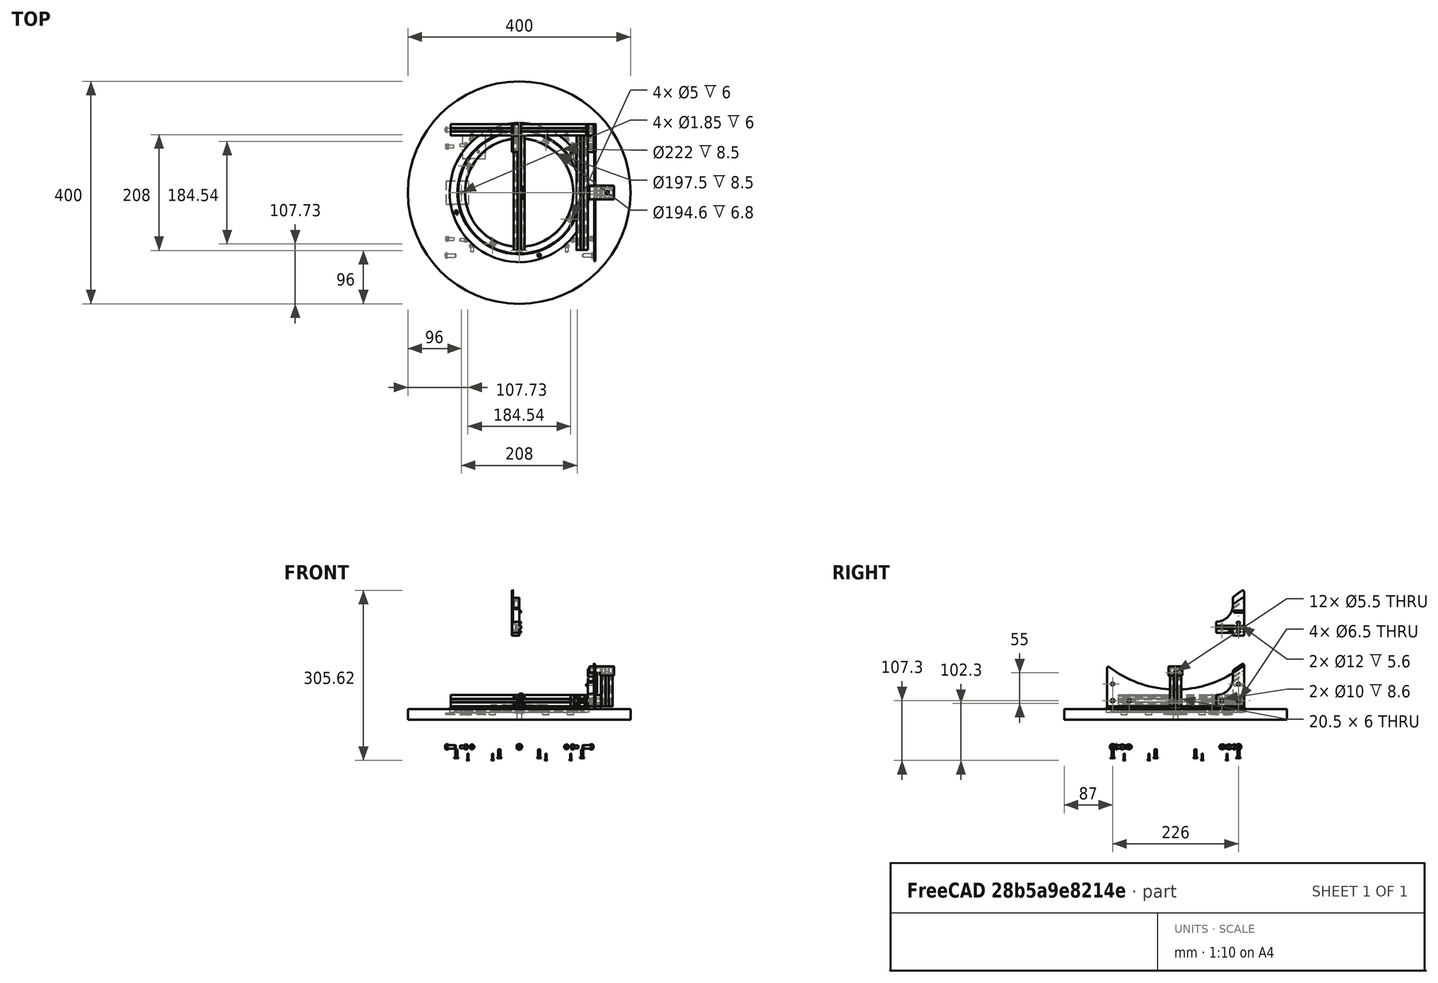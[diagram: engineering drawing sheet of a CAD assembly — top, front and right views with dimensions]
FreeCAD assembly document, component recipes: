
FREECAD ASSEMBLY — COMPONENT RECIPES ("Base")

This assembly document has 22 components, labeled P0..P21 below (a component is one placed body or linked part). 20 of them carry a construction recipe — the FreeCAD feature program that regenerates the part from scratch, quoted from this document or its linked companion documents; the rest are supplied as boundary geometry only. No exploded tour is included for this assembly.
NOTE — this tour is split across 2 documents so each fits a 32k-token context. This is document 1: the component sections continue in the remaining 1 document, each repeating the header above.
COMPONENT P0 — geometry summary ("SlewBearing"; no construction recipe available for this part):
  bounding box: 250.0 x 250.0 x 12.5 mm
  tessellated surface: 11,438 triangles
  volume: 155107 mm^3 (20% of its bounding box)
  symmetry: 4-fold rotationally symmetric about the z axis
COMPONENT P1 — recipe-attached ("RockerPost", modeled in this document).
Construction recipe (the document's own serialized feature program — sketch geometry with constraints, then the solid features built on it; lengths are millimeters unless a unit is written):

FEATURE [PartDesign::ShapeBinder] ShapeBinder012  label="RockerPost_Shapebinder_Rocker"
  Support = -> [Binder]
  TraceSupport = false
FEATURE [Sketcher::SketchObject] Sketch030  label="RockerPost_Sketch"
  ExternalGeometry = -> [ShapeBinder012]
  FullyConstrained = true
  MapMode = 5
  Placement = pos=(0,0,0) rot=(0.57735,0.57735,0.57735;2.0944rad)
  Support = -> [YZ_Plane030]
  sketch-geometry (6):
    g0: LineSegment StartX=103 StartY=43.562 StartZ=0 EndX=103 EndY=-15 EndZ=0
    g1: LineSegment StartX=103 StartY=-15 StartZ=0 EndX=123 EndY=-15 EndZ=0
    g2: LineSegment StartX=123 StartY=-15 StartZ=0 EndX=123 EndY=57.2946 EndZ=0
    g3: ArcOfCircle CenterX=0 CenterY=215 CenterZ=0 NormalX=0 NormalY=0 NormalZ=1 AngleXU=0 Radius=200 StartAngle=5.2534 EndAngle=5.37477
    g4: Circle CenterX=113 CenterY=30 CenterZ=0 NormalX=0 NormalY=0 NormalZ=1 AngleXU=0 Radius=2.75
    g5: Circle CenterX=113 CenterY=7.1e-15 CenterZ=0 NormalX=0 NormalY=0 NormalZ=1 AngleXU=0 Radius=3.25
  constraints (16):
    c: PointOnObject(g0,g-3)
    c: Vertical(g0)
    c: Coincident(g1,g0)
    c: Coincident(g2,g1)
    c: Vertical(g2)
    c: Coincident(g3,g-3)
    c: Coincident(g3,g0)
    c: Coincident(g3,g2)
    c: Symmetric(g0,g1,g-5)
    c: DistanceX(g1,g1) = 20
    c: DistanceY(g1) = -15
    c: DistanceY(g2,g2) = 72.2946  'PostHeight'
    c: Coincident(g4,g-6)
    c: Coincident(g5,g-5)
    c: Diameter(g5) = 6.5
    c: Diameter(g4) = 5.5
FEATURE [PartDesign::Pad] Pad016  label="RockerPost_Pillar"
  Direction = (1,-2e-16,3e-16)
  Length = 7
  Length2 = 5
  Midplane = true
  Placement = pos=(0,0,0) rot=(0.57735,0.57735,0.57735;2.0944rad)
  Profile = -> Sketch030
  Type = 4
  expr: Length = <<Common>>#<<Parameters>>.rail_width / 2 + 2
  expr: Length2 = <<Common>>#<<Parameters>>.rail_width / 2
FEATURE [PartDesign::CoordinateSystem] Local_CS042  label="LCS_RockerPost_H1"
  AttacherType = Attacher::AttachEngine3D
  MapMode = 11
  Placement = pos=(-5,113,6.1e-15) rot=(0.707107,0,-0.707107;3.14159rad)
  Support = -> [Pad016]
FEATURE [PartDesign::CoordinateSystem] Local_CS044  label="LCS_RockerPost_H2"
  AttacherType = Attacher::AttachEngine3D
  MapMode = 11
  Placement = pos=(7,113,9.1e-15) rot=(0.707107,0,0.707107;3.14159rad)
  Support = -> [Pad016]
FEATURE [PartDesign::Plane] DatumPlane010  label="RockerPost_DatumPlane_Top"
  AttachmentOffset = pos=(0,0,72.2946) rot=(0,0,1;0rad)
  Length = 427.613
  MapMode = 5
  Placement = pos=(-1.6e-14,2.52e-14,57.2946) rot=(0,0,-1;1.5708rad)
  ResizeMode = 0
  Support = -> [Pad016]
  Width = 78.2613
  expr: .AttachmentOffset.Base.z = Sketch030.Constraints.PostHeight
FEATURE [Sketcher::SketchObject] Sketch089  label="RockerPost_BraceHole_Sketch"
  ExternalGeometry = -> [Pad016]
  FullyConstrained = true
  MapMode = 5
  Placement = pos=(-5,0,0) rot=(0.57735,0.57735,-0.57735;4.18879rad)
  Support = -> [Pad016]
  expr: Constraints[1] = <<Common>>#<<Parameters>>.sidebolt
  sketch-geometry (1):
    g0: Circle CenterX=0 CenterY=30 CenterZ=0 NormalX=0 NormalY=0 NormalZ=1 AngleXU=0 Radius=2.5
  constraints (3):
    c: PointOnObject(g0,g-2)
    c: Diameter(g0) = 5
    c: DistanceY(g-3,g0) = 30
FEATURE [PartDesign::CoordinateSystem] Local_CS189  label="LCS_RockerBrace_H1"
  AttacherType = Attacher::AttachEngine3D
  MapMode = 11
  Placement = pos=(-5,113,30) rot=(0.707107,0,0.707107;3.14159rad)
  Support = -> [Pad016]
FEATURE [PartDesign::CoordinateSystem] Local_CS190  label="LCS_RockerBrace_H2"
  AttacherType = Attacher::AttachEngine3D
  MapMode = 11
  Placement = pos=(7,113,30) rot=(0.707107,0,0.707107;3.14159rad)
  Support = -> [Pad016]
FEATURE [PartDesign::Body] Body018  label="RockerPost"
  Group = -> [Sketch030,Pad016,Local_CS042,Local_CS044,DatumPlane010,Sketch089,Local_CS189,Local_CS190,ShapeBinder012]
  Origin = -> Origin030
  Placement = pos=(128,0,-132) rot=(0,0,1;0rad)
  Tip = -> Pad016
  expr: .Placement.Base.x = <<Common>>#<<Parameters>>.boxsize_x / 2 + <<Common>>#<<Parameters>>.rail_width / 2
  expr: .Placement.Base.z = <<Common>>#<<Parameters>>.datum_azbase
COMPONENT P2 — recipe-attached ("SidePlate", modeled in this document).
Construction recipe (the document's own serialized feature program — sketch geometry with constraints, then the solid features built on it; lengths are millimeters unless a unit is written):

FEATURE [PartDesign::CoordinateSystem] Local_CS217  label="LCS_SidePlate_ArmSlot"
  AttacherType = Attacher::AttachEngine3D
  AttachmentOffset = pos=(0,-5,1) rot=(0,0,1;1.5708rad)
  MapMode = 5
  Placement = pos=(1,-1.3e-15,-5) rot=(0.707107,0,0.707107;3.14159rad)
  Support = -> [YZ_Plane032]
  expr: .AttachmentOffset.Base.z = <<Common>>#<<Parameters>>.rocker_plate / 2
FEATURE [PartDesign::Plane] DatumPlane029  label="SidePlate_DatumPlane_P"
  AttachmentOffset = pos=(0,0,2) rot=(0,0,1;0rad)
  Length = 275.092
  MapMode = 5
  Placement = pos=(2,-4e-16,4e-16) rot=(0.57735,0.57735,0.57735;2.0944rad)
  ResizeMode = 0
  Support = -> [YZ_Plane032]
  Width = 115.103
  expr: .AttachmentOffset.Base.z = <<Common>>#<<Parameters>>.rocker_plate
FEATURE [PartDesign::CoordinateSystem] Local_CS059  label="LCS_SidePlate_PostAP"
  AttacherType = Attacher::AttachEngine3D
  AttachmentOffset = pos=(113,-5,0) rot=(0,0,1;1.5708rad)
  MapMode = 5
  Placement = pos=(2,113,-5) rot=(0.707107,0,0.707107;3.14159rad)
  Support = -> [DatumPlane029]
  expr: .AttachmentOffset.Base.x = <<Common>>#<<Parameters>>.bolt_y
FEATURE [PartDesign::CoordinateSystem] Local_CS063  label="LCS_SidePlate_PostFP"
  AttacherType = Attacher::AttachEngine3D
  AttachmentOffset = pos=(-113,-5,0) rot=(0,0,1;1.5708rad)
  MapMode = 5
  Placement = pos=(2,-113,-5) rot=(0.707107,0,0.707107;3.14159rad)
  Support = -> [DatumPlane029]
  expr: .AttachmentOffset.Base.x = -<<Common>>#<<Parameters>>.bolt_y
FEATURE [PartDesign::CoordinateSystem] Local_CS110  label="LCS_SidePlate_BraceAP"
  AttacherType = Attacher::AttachEngine3D
  AttachmentOffset = pos=(83,-5,0) rot=(0,0,1;1.5708rad)
  MapMode = 5
  Placement = pos=(2,83,-5) rot=(0.707107,0,0.707107;3.14159rad)
  Support = -> [DatumPlane029]
  expr: .AttachmentOffset.Base.x = <<Common>>#<<Parameters>>.bolt_y - 30
FEATURE [PartDesign::CoordinateSystem] Local_CS112  label="LCS_SidePlate_BraceFP"
  AttacherType = Attacher::AttachEngine3D
  AttachmentOffset = pos=(-83,-5,0) rot=(0,0,1;1.5708rad)
  MapMode = 5
  Placement = pos=(2,-83,-5) rot=(0.707107,0,0.707107;3.14159rad)
  Support = -> [DatumPlane029]
  expr: .AttachmentOffset.Base.x = -<<Common>>#<<Parameters>>.bolt_y + 30
FEATURE [PartDesign::CoordinateSystem] Local_CS182  label="LCS_SidePlate_PBrace_AP"
  AttacherType = Attacher::AttachEngine3D
  AttachmentOffset = pos=(113,25,0) rot=(0,0,1;1.5708rad)
  MapMode = 5
  Placement = pos=(2,113,25) rot=(0.707107,0,0.707107;3.14159rad)
  Support = -> [DatumPlane029]
  expr: .AttachmentOffset.Base.x = <<Common>>#<<Parameters>>.bolt_y
FEATURE [PartDesign::CoordinateSystem] Local_CS184  label="LCS_SidePlate_PBrace_FP"
  AttacherType = Attacher::AttachEngine3D
  AttachmentOffset = pos=(-113,25,0) rot=(0,0,1;1.5708rad)
  MapMode = 5
  Placement = pos=(2,-113,25) rot=(0.707107,0,0.707107;3.14159rad)
  Support = -> [DatumPlane029]
  expr: .AttachmentOffset.Base.x = -<<Common>>#<<Parameters>>.bolt_y
FEATURE [PartDesign::Plane] DatumPlane030  label="SidePlate_DatumPlane_S"
  Length = 275.092
  MapMode = 5
  Placement = pos=(0,0,0) rot=(0.57735,0.57735,0.57735;2.0944rad)
  ResizeMode = 0
  Support = -> [YZ_Plane032]
  Width = 115.103
FEATURE [PartDesign::CoordinateSystem] Local_CS061  label="LCS_SidePlate_PostAS"
  AttacherType = Attacher::AttachEngine3D
  AttachmentOffset = pos=(-113,-5,0) rot=(0,0,1;1.5708rad)
  MapMode = 5
  Placement = pos=(1.31e-14,113,-5) rot=(0,1,0;4.71239rad)
  Support = -> [DatumPlane030]
  expr: .AttachmentOffset.Base.x = -<<Common>>#<<Parameters>>.bolt_y
FEATURE [PartDesign::CoordinateSystem] Local_CS065  label="LCS_SidePlate_PostFS"
  AttacherType = Attacher::AttachEngine3D
  AttachmentOffset = pos=(113,-5,0) rot=(0,0,1;1.5708rad)
  MapMode = 5
  Placement = pos=(-1.2e-14,-113,-5) rot=(0,1,0;4.71239rad)
  Support = -> [DatumPlane030]
  expr: .AttachmentOffset.Base.x = <<Common>>#<<Parameters>>.bolt_y
FEATURE [PartDesign::CoordinateSystem] Local_CS111  label="LCS_SidePlate_BraceAS"
  AttacherType = Attacher::AttachEngine3D
  AttachmentOffset = pos=(-83,-5,0) rot=(0,0,1;1.5708rad)
  MapMode = 5
  Placement = pos=(9.8e-15,83,-5) rot=(0,1,0;4.71239rad)
  Support = -> [DatumPlane030]
  expr: .AttachmentOffset.Base.x = -<<Common>>#<<Parameters>>.bolt_y + 30
FEATURE [PartDesign::CoordinateSystem] Local_CS113  label="LCS_SidePlate_BraceFS"
  AttacherType = Attacher::AttachEngine3D
  AttachmentOffset = pos=(83,-5,0) rot=(0,0,1;1.5708rad)
  MapMode = 5
  Placement = pos=(-8.7e-15,-83,-5) rot=(0,1,0;4.71239rad)
  Support = -> [DatumPlane030]
  expr: .AttachmentOffset.Base.x = <<Common>>#<<Parameters>>.bolt_y - 30
FEATURE [PartDesign::CoordinateSystem] Local_CS183  label="LCS_SidePlate_PBrace_AS"
  AttacherType = Attacher::AttachEngine3D
  AttachmentOffset = pos=(-113,25,0) rot=(0,0,1;1.5708rad)
  MapMode = 5
  Placement = pos=(9.8e-15,113,25) rot=(0,1,0;4.71239rad)
  Support = -> [DatumPlane030]
  expr: .AttachmentOffset.Base.x = -<<Common>>#<<Parameters>>.bolt_y
FEATURE [PartDesign::CoordinateSystem] Local_CS185  label="LCS_SidePlate_PBrace_FS"
  AttacherType = Attacher::AttachEngine3D
  AttachmentOffset = pos=(113,25,0) rot=(0,0,1;1.5708rad)
  MapMode = 5
  Placement = pos=(-1.53e-14,-113,25) rot=(0,1,0;4.71239rad)
  Support = -> [DatumPlane030]
  expr: .AttachmentOffset.Base.x = <<Common>>#<<Parameters>>.bolt_y
FEATURE [Sketcher::SketchObject] Sketch274  label="RockerSide_MasterSketch"
  FullyConstrained = true
  MapMode = 5
  Placement = pos=(0,0,0) rot=(0.57735,0.57735,0.57735;2.0944rad)
  Support = -> [YZ_Plane032]
  expr: Constraints[12] = <<Common>>#<<Parameters>>.datum_lowercell - <<Common>>#<<Parameters>>.datum_rocker_z
  expr: Constraints[13] = <<Common>>#<<Parameters>>.bolt_y
  expr: Constraints[1] = <<Common>>#<<Parameters>>.rail_dia
  expr: Constraints[2] = <<Common>>#<<Parameters>>.datum_rocker_z - <<Common>>#<<Parameters>>.datum_azbase
  expr: Constraints[33] = <<Common>>#<<Parameters>>.rail_dia - <<Common>>#<<Parameters>>.rail_height * 2
  expr: Constraints[6] = <<Common>>#<<Parameters>>.bolt_y
  sketch-geometry (14):
    g0: Circle CenterX=0 CenterY=215 CenterZ=0 NormalX=0 NormalY=0 NormalZ=1 AngleXU=0 Radius=200
    g1: Circle CenterX=0 CenterY=0 CenterZ=0 NormalX=0 NormalY=0 NormalZ=1 AngleXU=0 Radius=2.5
    g2: Circle CenterX=-113 CenterY=0 CenterZ=0 NormalX=0 NormalY=0 NormalZ=1 AngleXU=0 Radius=3
    g3: Circle CenterX=113 CenterY=0 CenterZ=0 NormalX=0 NormalY=0 NormalZ=1 AngleXU=0 Radius=3
    g4: Circle CenterX=113 CenterY=30 CenterZ=0 NormalX=0 NormalY=0 NormalZ=1 AngleXU=0 Radius=2.5
    g5: Circle CenterX=-113 CenterY=30 CenterZ=0 NormalX=0 NormalY=0 NormalZ=1 AngleXU=0 Radius=2.5
    g6: Circle CenterX=-113 CenterY=70 CenterZ=0 NormalX=0 NormalY=0 NormalZ=1 AngleXU=0 Radius=2.5
    g7: Circle CenterX=0 CenterY=31.1686 CenterZ=0 NormalX=0 NormalY=0 NormalZ=1 AngleXU=0 Radius=2.5
    g8: Circle CenterX=113 CenterY=70 CenterZ=0 NormalX=0 NormalY=0 NormalZ=1 AngleXU=0 Radius=2.5
    g9: Circle CenterX=0 CenterY=215 CenterZ=0 NormalX=0 NormalY=0 NormalZ=1 AngleXU=0 Radius=183.831
    g10: GeomPoint X=113 Y=70 Z=0
    g11: LineSegment StartX=-113 StartY=0 StartZ=0 EndX=-113 EndY=70 EndZ=0
    g12: LineSegment StartX=113 StartY=0 StartZ=0 EndX=113 EndY=70 EndZ=0
    g13: Circle CenterX=0 CenterY=215 CenterZ=0 NormalX=0 NormalY=0 NormalZ=1 AngleXU=0 Radius=165
  constraints (34):
    c: PointOnObject(g0,g-2)
    c: Diameter(g0) = 400
    c: DistanceY(g0) = 215
    c: Coincident(g1,g-1)
    c: PointOnObject(g3,g-1)
    c: PointOnObject(g7,g-2)
    c: DistanceX(g3) = 113
    c: Symmetric(g3,g2,g-2)
    c: Diameter(g2) = 6
    c: Equal(g2,g3)
    c: Coincident(g9,g0)
    c: PointOnObject(g10,g9)
    c: DistanceY(g0,g10) = -145
    c: DistanceX(g0,g10) = 113
    c: Diameter(g1) = 5
    c: Coincident(g11,g2)
    c: PointOnObject(g11,g9)
    c: Coincident(g12,g3)
    c: PointOnObject(g12,g9)
    c: Vertical(g12)
    c: Vertical(g11)
    c: PointOnObject(g5,g11)
    c: Coincident(g6,g11)
    c: PointOnObject(g7,g9)
    c: Coincident(g8,g12)
    c: Equal(g4,g8)
    c: Equal(g8,g7)
    c: Equal(g7,g6)
    c: Equal(g6,g5)
    c: Equal(g5,g1)
    c: Symmetric(g4,g5,g-2)
    c: DistanceY(g4) = 30
    c: Coincident(g13,g0)
    c: Diameter(g13) = 330
FEATURE [PartDesign::ShapeBinder] ShapeBinder011  label="SidePlate_ShapeBinder_Rocker"
  Support = -> [Binder]
  TraceSupport = false
FEATURE [Sketcher::SketchObject] Sketch035  label="SidePlate_Sketch"
  ExternalGeometry = -> [ShapeBinder011]
  FullyConstrained = true
  MapMode = 5
  Placement = pos=(0,0,0) rot=(0.57735,0.57735,0.57735;2.0944rad)
  Support = -> [YZ_Plane032]
  expr: Constraints[11] = <<Common>>#<<Parameters>>.rail_dia - 10
  expr: Constraints[16] = <<Common>>#<<Parameters>>.pri_fillet
  expr: Constraints[37] = <<Common>>#<<Parameters>>.pri_fillet
  expr: Constraints[5] = <<Common>>#<<Parameters>>.boxsize_y
  sketch-geometry (19):
    g0: LineSegment StartX=-123 StartY=-10 StartZ=0 EndX=123 EndY=-10 EndZ=0
    g1: LineSegment StartX=123 StartY=-10 StartZ=0 EndX=123 EndY=58.52 EndZ=0
    g2: LineSegment StartX=-123 StartY=58.52 StartZ=0 EndX=-123 EndY=-10 EndZ=0
    g3: LineSegment StartX=-113 StartY=1.42e-14 StartZ=0 EndX=113 EndY=1.25e-14 EndZ=0
    g4: Circle CenterX=-113 CenterY=1.42e-14 CenterZ=0 NormalX=0 NormalY=0 NormalZ=1 AngleXU=0 Radius=3.25
    g5: Circle CenterX=113 CenterY=1.25e-14 CenterZ=0 NormalX=0 NormalY=0 NormalZ=1 AngleXU=0 Radius=3.25
    g6: ArcOfCircle CenterX=-2.39e-14 CenterY=215 CenterZ=0 NormalX=0 NormalY=0 NormalZ=1 AngleXU=0 Radius=195 StartAngle=4.05617 EndAngle=5.36861
    g7: Circle CenterX=-83 CenterY=1.25e-14 CenterZ=0 NormalX=0 NormalY=0 NormalZ=1 AngleXU=0 Radius=2.75
    g8: Circle CenterX=83 CenterY=1.25e-14 CenterZ=0 NormalX=0 NormalY=0 NormalZ=1 AngleXU=0 Radius=2.75
    g9: ArcOfCircle CenterX=120.5 CenterY=58.52 CenterZ=0 NormalX=0 NormalY=0 NormalZ=1 AngleXU=0 Radius=2.5 StartAngle=1e-15 EndAngle=2.22702
    g10: Circle CenterX=113 CenterY=30 CenterZ=0 NormalX=0 NormalY=0 NormalZ=1 AngleXU=0 Radius=2.75
    g11: Circle CenterX=-113 CenterY=30 CenterZ=0 NormalX=0 NormalY=0 NormalZ=1 AngleXU=0 Radius=2.75
    g12: LineSegment StartX=-113 StartY=30 StartZ=0 EndX=-113 EndY=1.42e-14 EndZ=0
    g13: LineSegment StartX=-10.25 StartY=3 StartZ=0 EndX=10.25 EndY=3 EndZ=0
    g14: LineSegment StartX=10.25 StartY=3 StartZ=0 EndX=10.25 EndY=-3 EndZ=0
    g15: LineSegment StartX=10.25 StartY=-3 StartZ=0 EndX=-10.25 EndY=-3 EndZ=0
    g16: LineSegment StartX=-10.25 StartY=-3 StartZ=0 EndX=-10.25 EndY=3 EndZ=0
    g17: Circle CenterX=-113 CenterY=70 CenterZ=0 NormalX=0 NormalY=0 NormalZ=1 AngleXU=0 Radius=5.5
    g18: ArcOfCircle CenterX=-120.5 CenterY=58.52 CenterZ=0 NormalX=0 NormalY=0 NormalZ=1 AngleXU=0 Radius=2.5 StartAngle=0.914576 EndAngle=3.14159
  constraints (44):
    c: Coincident(g0,g1)
    c: Coincident(g2,g0)
    c: Vertical(g1)
    c: Vertical(g2)
    c: Symmetric(g0,g0,g-2)
    c: DistanceX(g0,g0) = 246
    c: Symmetric(g3,g3,g-2)
    c: Diameter(g4) = 6.5
    c: Symmetric(g5,g4,g-2)
    c: Symmetric(g7,g8,g-2)
    c: PointOnObject(g7,g3)
    c: Diameter(g6) = 390
    c: DistanceY(g0) = -10
    c: Coincident(g3,g4)
    c: Tangent(g6,g9) = 1.5708
    c: Tangent(g1,g9) = -1.5708
    c: Radius(g9) = 2.5
    c: DistanceX(g8,g5) = 30
    c: Symmetric(g11,g10,g-2)
    c: Equal(g10,g11)
    c: Coincident(g12,g11)
    c: Coincident(g12,g4)
    c: Coincident(g13,g14)
    c: Coincident(g14,g15)
    c: Coincident(g15,g16)
    c: Coincident(g16,g13)
    c: Horizontal(g13)
    c: Vertical(g14)
    c: DistanceX(g15,g15) = 20.5
    c: Symmetric(g14,g15,g-2)
    c: Symmetric(g15,g13,g3)
    c: DistanceY(g16,g16) = 6
    c: Equal(g10,g8)
    c: Equal(g8,g7)
    c: Diameter(g11) = 5.5
    c: Equal(g4,g5)
    c: Diameter(g17) = 11
    c: Radius(g18) = 2.5
    c: Tangent(g18,g2) = -1.5708
    c: Tangent(g18,g6) = 1.5708
    c: Coincident(g17,g-6)
    c: Coincident(g6,g-3)
    c: Coincident(g5,g-8)
    c: Coincident(g10,g-7)
FEATURE [PartDesign::Pad] Pad019  label="SidePlate_Pad"
  Direction = (1,-2e-16,3e-16)
  Length = 2
  Length2 = 100
  Placement = pos=(0,0,0) rot=(0.57735,0.57735,0.57735;2.0944rad)
  Profile = -> Sketch035
  Type = 0
  expr: Length = <<Common>>#<<Parameters>>.rocker_plate
FEATURE [PartDesign::Body] Body020  label="SidePlate"
  Group = -> [Sketch035,Pad019,Local_CS059,Local_CS061,Local_CS063,Local_CS065,Local_CS110,Local_CS111,Local_CS112,Local_CS113,Local_CS182,Local_CS183,Local_CS184,Local_CS185,Local_CS217,DatumPlane029,DatumPlane030,Sketch274,ShapeBinder011]
  Origin = -> Origin032
  Placement = pos=(135,0,-132) rot=(0,0,1;0rad)
  Tip = -> Pad019
  expr: .Placement.Base.x = <<Common>>#<<Parameters>>.boxsize_x / 2 + <<Common>>#<<Parameters>>.rail_width + 2
  expr: .Placement.Base.z = <<Common>>#<<Parameters>>.datum_azbase
COMPONENT P3 — recipe-attached ("ArmSpacer", modeled in this document).
Construction recipe (the document's own serialized feature program — sketch geometry with constraints, then the solid features built on it; lengths are millimeters unless a unit is written):

FEATURE [Sketcher::SketchObject] Sketch096  label="ArmSpacer_Sketch"
  FullyConstrained = true
  MapMode = 5
  Support = -> [XY_Plane069]
  expr: .Constraints.SpacerThick = <<Common>>#<<Parameters>>.alt_sideclamp
  sketch-geometry (12):
    g0: LineSegment StartX=-2 StartY=10 StartZ=0 EndX=11 EndY=10 EndZ=0
    g1: LineSegment StartX=11 StartY=10 StartZ=0 EndX=11 EndY=3 EndZ=0
    g2: LineSegment StartX=11 StartY=3 StartZ=0 EndX=12.5 EndY=3 EndZ=0
    g3: LineSegment StartX=12.5 StartY=3 StartZ=0 EndX=12.5 EndY=-3 EndZ=0
    g4: LineSegment StartX=12.5 StartY=-3 StartZ=0 EndX=11 EndY=-3 EndZ=0
    g5: LineSegment StartX=11 StartY=-3 StartZ=0 EndX=11 EndY=-10 EndZ=0
    g6: LineSegment StartX=11 StartY=-10 StartZ=0 EndX=-2 EndY=-10 EndZ=0
    g7: LineSegment StartX=-2 StartY=10 StartZ=0 EndX=-2 EndY=3 EndZ=0
    g8: LineSegment StartX=-2 StartY=3 StartZ=0 EndX=0 EndY=3 EndZ=0
    g9: LineSegment StartX=0 StartY=3 StartZ=0 EndX=0 EndY=-3 EndZ=0
    g10: LineSegment StartX=0 StartY=-3 StartZ=0 EndX=-2 EndY=-3 EndZ=0
    g11: LineSegment StartX=-2 StartY=-3 StartZ=0 EndX=-2 EndY=-10 EndZ=0
  constraints (35):
    c: Horizontal(g0)
    c: Vertical(g1)
    c: Coincident(g2,g1)
    c: Horizontal(g2)
    c: Coincident(g3,g2)
    c: Coincident(g4,g3)
    c: Coincident(g5,g4)
    c: Vertical(g5)
    c: Coincident(g6,g5)
    c: Horizontal(g6)
    c: Coincident(g0,g1)
    c: DistanceY(g3,g3) = 6
    c: Horizontal(g4)
    c: Equal(g6,g0)
    c: Symmetric(g2,g3,g-1)
    c: DistanceX(g1) = 11  'SpacerThick'
    c: DistanceX(g2,g2) = 1.5
    c: DistanceY(g5,g0) = 20
    c: Equal(g1,g5)
    c: Coincident(g7,g0)
    c: Vertical(g7)
    c: Coincident(g8,g7)
    c: PointOnObject(g8,g-2)
    c: Coincident(g9,g8)
    c: PointOnObject(g9,g-2)
    c: Coincident(g10,g9)
    c: Horizontal(g10)
    c: Coincident(g11,g10)
    c: Coincident(g11,g6)
    c: Vertical(g11)
    c: PointOnObject(g10,g7)
    c: DistanceX(g0,g-1) = 2
    c: PointOnObject(g8,g2)
    c: PointOnObject(g9,g4)
    c: Horizontal(g8)
FEATURE [PartDesign::Pad] Pad035  label="ArmSpacer_Base"
  Direction = (0,0,1)
  Length = 20
  Length2 = 100
  Midplane = true
  Profile = -> Sketch096
  Type = 0
FEATURE [Sketcher::SketchObject] Sketch097  label="ArmSpacer_Tab_Sketch"
  ExternalGeometry = -> [Pad035]
  FullyConstrained = true
  MapMode = 5
  Placement = pos=(0,0,0) rot=(1,0,0;1.5708rad)
  Support = -> [XZ_Plane069]
  sketch-geometry (14):
    g0: LineSegment StartX=0 StartY=-3 StartZ=0 EndX=0 EndY=-10 EndZ=0
    g1: LineSegment StartX=0 StartY=-10 StartZ=0 EndX=-2 EndY=-10 EndZ=0
    g2: LineSegment StartX=-2 StartY=-10 StartZ=0 EndX=-2 EndY=-3 EndZ=0
    g3: LineSegment StartX=-2 StartY=-3 StartZ=0 EndX=0 EndY=-3 EndZ=0
    g4: LineSegment StartX=-2 StartY=10 StartZ=0 EndX=0 EndY=10 EndZ=0
    g5: LineSegment StartX=0 StartY=10 StartZ=0 EndX=0 EndY=3 EndZ=0
    g6: LineSegment StartX=0 StartY=3 StartZ=0 EndX=-2 EndY=3 EndZ=0
    g7: LineSegment StartX=-2 StartY=3 StartZ=0 EndX=-2 EndY=10 EndZ=0
    g8: LineSegment StartX=11 StartY=3 StartZ=0 EndX=12.5 EndY=3 EndZ=0
    g9: LineSegment StartX=12.5 StartY=3 StartZ=0 EndX=12.5 EndY=-3 EndZ=0
    g10: LineSegment StartX=12.5 StartY=-3 StartZ=0 EndX=11 EndY=-3 EndZ=0
    g11: LineSegment StartX=11 StartY=-3 StartZ=0 EndX=11 EndY=3 EndZ=0
    g12: LineSegment StartX=0 StartY=3 StartZ=0 EndX=11 EndY=3 EndZ=0
    g13: LineSegment StartX=0 StartY=-3 StartZ=0 EndX=11 EndY=-3 EndZ=0
  constraints (37):
    c: PointOnObject(g0,g-2)
    c: PointOnObject(g0,g-2)
    c: Coincident(g1,g0)
    c: Coincident(g1,g-3)
    c: Coincident(g2,g1)
    c: PointOnObject(g2,g-3)
    c: Coincident(g3,g2)
    c: Coincident(g3,g0)
    c: Coincident(g4,g5)
    c: Coincident(g5,g6)
    c: Coincident(g6,g7)
    c: Coincident(g7,g4)
    c: Horizontal(g4)
    c: Horizontal(g6)
    c: Vertical(g5)
    c: Vertical(g7)
    c: Coincident(g4,g-3)
    c: PointOnObject(g5,g-2)
    c: Coincident(g8,g9)
    c: Coincident(g9,g10)
    c: Coincident(g10,g11)
    c: Coincident(g11,g8)
    c: Vertical(g9)
    c: PointOnObject(g8,g-4)
    c: PointOnObject(g9,g-5)
    c: Symmetric(g8,g10,g-1)
    c: DistanceY(g11,g11) = 6
    c: Coincident(g12,g5)
    c: Coincident(g12,g8)
    c: Coincident(g13,g0)
    c: Coincident(g13,g10)
    c: Horizontal(g13)
    c: Horizontal(g12)
    c: Horizontal(g1)
    c: Horizontal(g3)
    c: Parallel(g8,g10)
    c: Perpendicular(g-4,g8)
FEATURE [Sketcher::SketchObject] Sketch098  label="ArmSpacer_Hole_Sketch"
  FullyConstrained = true
  MapMode = 5
  Placement = pos=(0,0,0) rot=(0.57735,0.57735,0.57735;2.0944rad)
  Support = -> [YZ_Plane069]
  sketch-geometry (1):
    g0: Circle CenterX=0 CenterY=0 CenterZ=0 NormalX=0 NormalY=0 NormalZ=1 AngleXU=0 Radius=2.75
  constraints (2):
    c: Coincident(g0,g-1)
    c: Diameter(g0) = 5.5
FEATURE [PartDesign::Pocket] Pocket055  label="ArmSpacer_Tab"
  BaseFeature = -> Pad035
  Direction = (0,1,2e-16)
  Length = 5
  Length2 = 100
  Midplane = true
  Profile = -> Sketch097
  Type = 1
FEATURE [PartDesign::Pocket] Pocket056  label="ArmSpacer_Hole"
  BaseFeature = -> Pocket055
  Direction = (-1,2e-16,-3e-16)
  Length = 5
  Length2 = 100
  Midplane = true
  Profile = -> Sketch098
  Type = 1
FEATURE [PartDesign::CoordinateSystem] Local_CS212  label="LCS_ArmSpacer_I"
  AttacherType = Attacher::AttachEngine3D
  MapMode = 11
  Placement = pos=(0,0,1.8e-15) rot=(0.707107,0,0.707107;3.14159rad)
  Support = -> [Pocket056]
FEATURE [PartDesign::CoordinateSystem] Local_CS213  label="LCS_ArmSpacer_O"
  AttacherType = Attacher::AttachEngine3D
  MapMode = 11
  Placement = pos=(11,-2.2e-15,4.2e-15) rot=(0.707107,0,0.707107;3.14159rad)
  Support = -> [Pocket056]
FEATURE [PartDesign::Body] Body022016  label="ArmSpacer"
  Group = -> [Sketch096,Pad035,Sketch097,Sketch098,Local_CS212,Local_CS213,Pocket055,Pocket056]
  Origin = -> Origin069
  Placement = pos=(137,0,-132) rot=(0,0,1;0rad)
  Tip = -> Pocket056
  expr: .Placement.Base.x = <<Common>>#<<Parameters>>.bolt_x + <<Common>>#<<Parameters>>.rail_width + 12 + <<Common>>#<<Parameters>>.rocker_plate
  expr: .Placement.Base.z = <<Common>>#<<Parameters>>.datum_azbase
COMPONENT P4 — recipe-attached ("ArmPost", modeled in this document).
Construction recipe (the document's own serialized feature program — sketch geometry with constraints, then the solid features built on it; lengths are millimeters unless a unit is written):

FEATURE [Sketcher::SketchObject] Sketch099  label="ArmPost_Sketch"
  FullyConstrained = true
  MapMode = 5
  Support = -> [XY_Plane070]
  sketch-geometry (75):
    g0: LineSegment StartX=3 StartY=10 StartZ=0 EndX=3 EndY=8 EndZ=0
    g1: LineSegment StartX=3 StartY=8 StartZ=0 EndX=6 EndY=8 EndZ=0
    g2: LineSegment StartX=2.58579 StartY=4 StartZ=0 EndX=-2.58579 EndY=4 EndZ=0
    g3: LineSegment StartX=-6 StartY=8 StartZ=0 EndX=-3 EndY=8 EndZ=0
    g4: LineSegment StartX=-3 StartY=8 StartZ=0 EndX=-3 EndY=10 EndZ=0
    g5: Circle CenterX=0 CenterY=0 CenterZ=0 NormalX=0 NormalY=0 NormalZ=1 AngleXU=0 Radius=2.1
    g6: LineSegment StartX=-10 StartY=3 StartZ=0 EndX=-8 EndY=3 EndZ=0
    g7: LineSegment StartX=-8 StartY=3 StartZ=0 EndX=-8 EndY=6 EndZ=0
    g8: LineSegment StartX=-4 StartY=2.58579 StartZ=0 EndX=-4 EndY=-2.58579 EndZ=0
    g9: LineSegment StartX=-8 StartY=-6 StartZ=0 EndX=-8 EndY=-3 EndZ=0
    g10: LineSegment StartX=-8 StartY=-3 StartZ=0 EndX=-10 EndY=-3 EndZ=0
    g11: LineSegment StartX=-3 StartY=-10 StartZ=0 EndX=-3 EndY=-8 EndZ=0
    g12: LineSegment StartX=-3 StartY=-8 StartZ=0 EndX=-6 EndY=-8 EndZ=0
    g13: LineSegment StartX=-2.58579 StartY=-4 StartZ=0 EndX=2.58579 EndY=-4 EndZ=0
    g14: LineSegment StartX=6 StartY=-8 StartZ=0 EndX=3 EndY=-8 EndZ=0
    g15: LineSegment StartX=3 StartY=-8 StartZ=0 EndX=3 EndY=-10 EndZ=0
    g16: LineSegment StartX=10 StartY=-3 StartZ=0 EndX=8 EndY=-3 EndZ=0
    g17: LineSegment StartX=8 StartY=-3 StartZ=0 EndX=8 EndY=-6 EndZ=0
    g18: LineSegment StartX=8 StartY=-6 StartZ=0 EndX=7.41421 EndY=-6 EndZ=0
    g19: LineSegment StartX=7.41421 StartY=-6 StartZ=0 EndX=4 EndY=-2.58579 EndZ=0
    g20: LineSegment StartX=4 StartY=-2.58579 StartZ=0 EndX=4 EndY=2.58579 EndZ=0
    g21: LineSegment StartX=4 StartY=2.58579 StartZ=0 EndX=7.41421 EndY=6 EndZ=0
    g22: LineSegment StartX=7.41421 StartY=6 StartZ=0 EndX=8 EndY=6 EndZ=0
    g23: LineSegment StartX=8 StartY=6 StartZ=0 EndX=8 EndY=3 EndZ=0
    g24: LineSegment StartX=8 StartY=3 StartZ=0 EndX=10 EndY=3 EndZ=0
    g25: LineSegment StartX=6 StartY=8 StartZ=0 EndX=6 EndY=7.41421 EndZ=0
    g26: LineSegment StartX=6 StartY=7.41421 StartZ=0 EndX=2.58579 EndY=4 EndZ=0
    g27: LineSegment StartX=-2.58579 StartY=4 StartZ=0 EndX=-6 EndY=7.41421 EndZ=0
    g28: LineSegment StartX=-6 StartY=7.41421 StartZ=0 EndX=-6 EndY=8 EndZ=0
    g29: LineSegment StartX=-8 StartY=6 StartZ=0 EndX=-7.41421 EndY=6 EndZ=0
    g30: LineSegment StartX=-7.41421 StartY=6 StartZ=0 EndX=-4 EndY=2.58579 EndZ=0
    g31: LineSegment StartX=-4 StartY=-2.58579 StartZ=0 EndX=-7.41421 EndY=-6 EndZ=0
    g32: LineSegment StartX=-7.41421 StartY=-6 StartZ=0 EndX=-8 EndY=-6 EndZ=0
    g33: LineSegment StartX=-2.58579 StartY=-4 StartZ=0 EndX=-6 EndY=-7.41421 EndZ=0
    g34: LineSegment StartX=-6 StartY=-7.41421 StartZ=0 EndX=-6 EndY=-8 EndZ=0
    g35: LineSegment StartX=2.58579 StartY=-4 StartZ=0 EndX=6 EndY=-7.41421 EndZ=0
    g36: LineSegment StartX=6 StartY=-7.41421 StartZ=0 EndX=6 EndY=-8 EndZ=0
    g37: LineSegment StartX=-4 StartY=2.58579 StartZ=0 EndX=-2.58579 EndY=4 EndZ=0
    g38: LineSegment StartX=-7.41421 StartY=7.41421 StartZ=0 EndX=7.41421 EndY=7.41421 EndZ=0
    g39: LineSegment StartX=7.41421 StartY=7.41421 StartZ=0 EndX=7.41421 EndY=-7.41421 EndZ=0
    g40: LineSegment StartX=7.41421 StartY=-7.41421 StartZ=0 EndX=-7.41421 EndY=-7.41421 EndZ=0
    g41: LineSegment StartX=-7.41421 StartY=-7.41421 StartZ=0 EndX=-7.41421 EndY=7.41421 EndZ=0
    g42: LineSegment StartX=-10 StartY=10 StartZ=0 EndX=10 EndY=10 EndZ=0
    g43: LineSegment StartX=10 StartY=10 StartZ=0 EndX=10 EndY=-10 EndZ=0
    g44: LineSegment StartX=10 StartY=-10 StartZ=0 EndX=-10 EndY=-10 EndZ=0
    g45: LineSegment StartX=-10 StartY=-10 StartZ=0 EndX=-10 EndY=10 EndZ=0
    g46: LineSegment StartX=4 StartY=4 StartZ=0 EndX=-4 EndY=4 EndZ=0
    g47: LineSegment StartX=-4 StartY=4 StartZ=0 EndX=-4 EndY=-4 EndZ=0
    g48: LineSegment StartX=-4 StartY=-4 StartZ=0 EndX=4 EndY=-4 EndZ=0
    g49: LineSegment StartX=4 StartY=-4 StartZ=0 EndX=4 EndY=4 EndZ=0
    g50: LineSegment StartX=-10 StartY=-10 StartZ=0 EndX=10 EndY=10 EndZ=0
    g51: LineSegment StartX=-10 StartY=10 StartZ=0 EndX=10 EndY=-10 EndZ=0
    g52: LineSegment StartX=2.58579 StartY=4 StartZ=0 EndX=4 EndY=2.58579 EndZ=0
    g53: LineSegment StartX=2.58579 StartY=-4 StartZ=0 EndX=4 EndY=-2.58579 EndZ=0
    g54: LineSegment StartX=-4 StartY=-2.58579 StartZ=0 EndX=-2.58579 EndY=-4 EndZ=0
    g55: LineSegment StartX=10 StartY=3 StartZ=0 EndX=3 EndY=10 EndZ=0
    g56: LineSegment StartX=-3 StartY=10 StartZ=0 EndX=-10 EndY=3 EndZ=0
    g57: LineSegment StartX=-10 StartY=-3 StartZ=0 EndX=-3 EndY=-10 EndZ=0
    g58: LineSegment StartX=3 StartY=-10 StartZ=0 EndX=10 EndY=-3 EndZ=0
    g59: ArcOfCircle CenterX=-9 CenterY=9 CenterZ=0 NormalX=0 NormalY=0 NormalZ=1 AngleXU=0 Radius=1 StartAngle=1.57078 EndAngle=3.14161
    g60: ArcOfCircle CenterX=9 CenterY=9 CenterZ=0 NormalX=0 NormalY=0 NormalZ=1 AngleXU=0 Radius=1 StartAngle=6.28316 EndAngle=7.854
    g61: ArcOfCircle CenterX=9 CenterY=-9 CenterZ=0 NormalX=0 NormalY=0 NormalZ=1 AngleXU=0 Radius=1 StartAngle=4.71238 EndAngle=6.28319
    g62: ArcOfCircle CenterX=-9 CenterY=-9 CenterZ=0 NormalX=0 NormalY=0 NormalZ=1 AngleXU=0 Radius=1 StartAngle=3.14159 EndAngle=4.71241
    g63: LineSegment StartX=-10 StartY=-9 StartZ=0 EndX=10 EndY=-9 EndZ=0
    g64: LineSegment StartX=-10 StartY=8.99998 StartZ=0 EndX=10 EndY=8.99998 EndZ=0
    g65: LineSegment StartX=-8.99998 StartY=10 StartZ=0 EndX=-8.99998 EndY=-10 EndZ=0
    g66: LineSegment StartX=8.99999 StartY=10 StartZ=0 EndX=8.99999 EndY=-10 EndZ=0
    g67: LineSegment StartX=-10 StartY=8.99998 StartZ=0 EndX=-10 EndY=3 EndZ=0
    g68: LineSegment StartX=-10 StartY=-3 StartZ=0 EndX=-10 EndY=-9 EndZ=0
    g69: LineSegment StartX=-8.99998 StartY=10 StartZ=0 EndX=-3 EndY=10 EndZ=0
    g70: LineSegment StartX=8.99999 StartY=10 StartZ=0 EndX=3 EndY=10 EndZ=0
    g71: LineSegment StartX=10 StartY=8.99998 StartZ=0 EndX=10 EndY=3 EndZ=0
    g72: LineSegment StartX=10 StartY=-9 StartZ=0 EndX=10 EndY=-3 EndZ=0
    g73: LineSegment StartX=8.99999 StartY=-10 StartZ=0 EndX=3 EndY=-10 EndZ=0
    g74: LineSegment StartX=-8.99998 StartY=-10 StartZ=0 EndX=-3 EndY=-10 EndZ=0
  constraints (212):
    c: Diameter(g5) = 4.2
    c: Coincident(g42,g43)
    c: Coincident(g43,g44)
    c: Coincident(g44,g45)
    c: Coincident(g45,g42)
    c: Horizontal(g44)
    c: Vertical(g45)
    c: Symmetric(g42,g43,g-1)
    c: Symmetric(g42,g42,g-2)
    c: Coincident(g5,g-1)
    c: Coincident(g38,g41)
    c: Coincident(g7,g29)
    c: Coincident(g29,g30)
    c: Coincident(g27,g28)
    c: Coincident(g3,g28)
    c: Coincident(g3,g4)
    c: Coincident(g6,g7)
    c: Coincident(g2,g27)
    c: Coincident(g2,g37)
    c: Coincident(g8,g30)
    c: Coincident(g8,g37)
    c: Coincident(g8,g31)
    c: Coincident(g13,g33)
    c: Coincident(g9,g10)
    c: Coincident(g11,g12)
    c: Coincident(g12,g34)
    c: Coincident(g33,g34)
    c: Coincident(g40,g41)
    c: Coincident(g31,g32)
    c: Coincident(g9,g32)
    c: Coincident(g14,g36)
    c: Coincident(g17,g18)
    c: Coincident(g39,g40)
    c: Coincident(g18,g19)
    c: Coincident(g35,g36)
    c: Coincident(g13,g35)
    c: Coincident(g19,g20)
    c: Coincident(g16,g17)
    c: Coincident(g0,g1)
    c: Coincident(g1,g25)
    c: Coincident(g22,g23)
    c: Coincident(g23,g24)
    c: Coincident(g21,g22)
    c: Coincident(g38,g39)
    c: Coincident(g25,g26)
    c: Coincident(g2,g26)
    c: Coincident(g20,g21)
    c: Horizontal(g1)
    c: Horizontal(g3)
    c: Horizontal(g12)
    c: Horizontal(g14)
    c: Vertical(g34)
    c: Vertical(g11)
    c: Vertical(g15)
    c: Vertical(g36)
    c: Vertical(g4)
    c: Vertical(g0)
    c: Vertical(g28)
    c: Vertical(g25)
    c: Vertical(g7)
    c: Vertical(g9)
    c: Vertical(g23)
    c: Vertical(g17)
    c: Horizontal(g29)
    c: Horizontal(g6)
    c: Horizontal(g10)
    c: Horizontal(g32)
    c: Horizontal(g22)
    c: Horizontal(g24)
    c: Horizontal(g16)
    c: Horizontal(g18)
    c: Parallel(g30,g27)
    c: Parallel(g27,g35)
    c: Parallel(g35,g19)
    c: Parallel(g21,g26)
    c: Parallel(g31,g33)
    c: Coincident(g46,g47)
    c: Coincident(g47,g48)
    c: Coincident(g48,g49)
    c: Coincident(g49,g46)
    c: Horizontal(g46)
    c: Horizontal(g48)
    c: Vertical(g47)
    c: Vertical(g49)
    c: Horizontal(g2)
    c: Horizontal(g13)
    c: Vertical(g8)
    c: Vertical(g20)
    c: PointOnObject(g2,g46)
    c: PointOnObject(g19,g49)
    c: PointOnObject(g13,g48)
    c: PointOnObject(g8,g47)
    c: Coincident(g50,g44)
    c: Coincident(g50,g42)
    c: Coincident(g51,g42)
    c: Coincident(g51,g43)
    c: PointOnObject(g39,g51)
    c: PointOnObject(g38,g50)
    c: PointOnObject(g38,g51)
    c: Vertical(g39)
    c: Vertical(g41)
    c: Horizontal(g38)
    c: Horizontal(g40)
    c: PointOnObject(g46,g50)
    c: PointOnObject(g46,g51)
    c: PointOnObject(g48,g51)
    c: Parallel(g27,g51)
    c: Parallel(g26,g50)
    c: Perpendicular(g51,g37)
    c: Parallel(g31,g26)
    c: PointOnObject(g4,g42)
    c: PointOnObject(g24,g43)
    c: PointOnObject(g6,g45)
    c: PointOnObject(g10,g45)
    c: PointOnObject(g29,g41)
    c: PointOnObject(g31,g41)
    c: PointOnObject(g33,g40)
    c: PointOnObject(g35,g40)
    c: PointOnObject(g18,g39)
    c: PointOnObject(g21,g39)
    c: PointOnObject(g25,g38)
    c: PointOnObject(g27,g38)
    c: Coincident(g52,g2)
    c: Coincident(g52,g20)
    c: Coincident(g53,g13)
    c: Coincident(g53,g19)
    c: Coincident(g54,g8)
    c: Coincident(g54,g13)
    c: Perpendicular(g50,g54)
    c: Perpendicular(g51,g53)
    c: Perpendicular(g50,g52)
    c: Equal(g37,g52)
    c: Equal(g52,g53)
    c: Equal(g53,g54)
    c: Distance(g37) = 2
    c: Coincident(g14,g15)
    c: PointOnObject(g6,g24)
    c: PointOnObject(g9,g16)
    c: PointOnObject(g11,g4)
    c: PointOnObject(g14,g0)
    c: PointOnObject(g11,g44)
    c: PointOnObject(g15,g44)
    c: DistanceX(g42) = 10
    c: DistanceY(g49,g49) = 8
    c: DistanceY(g18,g21) = 12
    c: Coincident(g56,g4)
    c: Coincident(g57,g10)
    c: Coincident(g58,g15)
    c: Perpendicular(g51,g58)
    c: Perpendicular(g50,g55)
    c: Perpendicular(g51,g56)
    c: Equal(g58,g57)
    c: Equal(g57,g55)
    c: DistanceY(g16,g24) = 6
    c: Equal(g42,g43)
    c: Coincident(g55,g0)
    c: Coincident(g55,g24)
    c: Coincident(g56,g6)
    c: Coincident(g11,g57)
    c: Coincident(g16,g58)
    c: DistanceX(g6,g6) = 2
    c: Equal(g6,g10)
    c: Equal(g10,g24)
    c: Equal(g24,g16)
    c: Equal(g16,g15)
    c: Equal(g15,g11)
    c: Equal(g11,g4)
    c: Equal(g4,g0)
    c: PointOnObject(g59,g51)
    c: PointOnObject(g59,g45)
    c: PointOnObject(g59,g42)
    c: PointOnObject(g60,g42)
    c: PointOnObject(g60,g43)
    c: PointOnObject(g61,g51)
    c: PointOnObject(g61,g43)
    c: PointOnObject(g61,g44)
    c: PointOnObject(g62,g50)
    c: PointOnObject(g62,g44)
    c: PointOnObject(g62,g45)
    c: Radius(g62) = 1
    c: Equal(g62,g59)
    c: Equal(g59,g60)
    c: Equal(g60,g61)
    c: Coincident(g63,g62)
    c: Coincident(g63,g61)
    c: Horizontal(g63)
    c: Coincident(g64,g59)
    c: Coincident(g64,g60)
    c: Horizontal(g64)
    c: Coincident(g65,g59)
    c: Coincident(g65,g62)
    c: Vertical(g65)
    c: Coincident(g66,g60)
    c: Coincident(g66,g61)
    c: Vertical(g66)
    c: PointOnObject(g62,g63)
    c: Coincident(g67,g59)
    c: Coincident(g67,g6)
    c: Coincident(g68,g10)
    c: Coincident(g68,g62)
    c: Coincident(g69,g59)
    c: Coincident(g69,g4)
    c: Coincident(g70,g60)
    c: Coincident(g70,g0)
    c: Coincident(g71,g60)
    c: Coincident(g71,g24)
    c: Coincident(g72,g61)
    c: Coincident(g72,g16)
    c: Coincident(g73,g61)
    c: Coincident(g73,g15)
    c: Coincident(g74,g62)
    c: Coincident(g74,g11)
FEATURE [PartDesign::Pad] Pad037  label="ArmPost_Pad"
  Direction = (0,0,1)
  Length = 70
  Length2 = 100
  Profile = -> Sketch099
  Type = 0
  expr: Length = <<Common>>#<<Parameters>>.datum_rocker_z - <<Common>>#<<Parameters>>.datum_azbase + 15 - <<Common>>#<<Parameters>>.rail_dia / 2 + <<Common>>#<<Parameters>>.rail_height + 5
FEATURE [Sketcher::SketchObject] Sketch100  label="ArmPost_Hole_Sketch"
  ExternalGeometry = -> [Pad037]
  FullyConstrained = true
  MapMode = 5
  Placement = pos=(4,0,0) rot=(0.57735,0.57735,0.57735;2.0944rad)
  Support = -> [Pad037]
  sketch-geometry (2):
    g0: Circle CenterX=0 CenterY=10 CenterZ=0 NormalX=0 NormalY=0 NormalZ=1 AngleXU=0 Radius=2.75
    g1: Circle CenterX=0 CenterY=60 CenterZ=0 NormalX=0 NormalY=0 NormalZ=1 AngleXU=0 Radius=2.75
  constraints (6):
    c: PointOnObject(g0,g-2)
    c: PointOnObject(g1,g-2)
    c: Diameter(g1) = 5.5
    c: Equal(g1,g0)
    c: DistanceY(g0) = 10
    c: DistanceY(g1,g-3) = 10
FEATURE [PartDesign::Pocket] Pocket039  label="ArmPost_Hole"
  BaseFeature = -> Pad037
  Direction = (-1,0,0)
  Length = 5
  Length2 = 100
  Midplane = true
  Profile = -> Sketch100
  Type = 1
FEATURE [PartDesign::CoordinateSystem] Local_CS214  label="LCS_ArmPole_Upper"
  AttacherType = Attacher::AttachEngine3D
  AttachmentOffset = pos=(0,0,-10) rot=(-0.57735,-0.57735,-0.57735;2.0944rad)
  MapMode = 11
  Placement = pos=(0,0,60) rot=(0,-1,0;1.5708rad)
  Support = -> [Pocket039]
FEATURE [PartDesign::CoordinateSystem] Local_CS215  label="LCS_ArmPole_Lower"
  AttacherType = Attacher::AttachEngine3D
  AttachmentOffset = pos=(0,0,10) rot=(-0.57735,-0.57735,-0.57735;2.0944rad)
  MapMode = 11
  Placement = pos=(0,0,10) rot=(0,-1,0;1.5708rad)
  Support = -> [Pocket039]
FEATURE [PartDesign::Body] Body022017  label="ArmPost"
  Group = -> [Sketch099,Pad037,Sketch100,Pocket039,Local_CS214,Local_CS215]
  Origin = -> Origin070
  Placement = pos=(158,0,-142) rot=(0,0,1;0rad)
  Tip = -> Pocket039
  expr: .Placement.Base.x = <<Common>>#<<Parameters>>.bolt_x + <<Common>>#<<Parameters>>.rail_width + <<Common>>#<<Parameters>>.alt_sideclamp + 2 + <<Common>>#<<Parameters>>.rocker_plate + 20
  expr: .Placement.Base.z = <<Common>>#<<Parameters>>.datum_azbase - 10
COMPONENT P5 — recipe-attached ("AzimuthBase", modeled in this document).
Construction recipe (the document's own serialized feature program — sketch geometry with constraints, then the solid features built on it; lengths are millimeters unless a unit is written):

FEATURE [PartDesign::AdditiveCylinder] Cylinder006  label="AzimuthBaseCylinder"
  Angle = 360
  AttacherType = Attacher::AttachEngine3D
  AttachmentOffset = pos=(0,0,-19.05) rot=(0,0,1;0rad)
  FirstAngle = 0
  Height = 19.05
  MapMode = 5
  Placement = pos=(0,0,-19.05) rot=(0,0,1;0rad)
  Radius = 200
  SecondAngle = 0
  Support = -> [XY_Plane073]
  expr: Radius = max(<<Common>>#<<Parameters>>.rail_dia; <<Common>>#<<Parameters>>.azi_basesize) / 2
FEATURE [Sketcher::SketchObject] Sketch105  label="AzimuthBase_Nut_Sketch"
  FullyConstrained = true
  MapMode = 5
  Placement = pos=(0,0,3.6e-15) rot=(0,0,1;0rad)
  Support = -> [Cylinder006]
  sketch-geometry (9):
    g0: LineSegment StartX=3.81051 StartY=-6.6 StartZ=0 EndX=7.62102 EndY=0 EndZ=0
    g1: LineSegment StartX=7.62102 StartY=0 StartZ=0 EndX=3.81051 EndY=6.6 EndZ=0
    g2: LineSegment StartX=3.81051 StartY=6.6 StartZ=0 EndX=-3.81051 EndY=6.6 EndZ=0
    g3: LineSegment StartX=-3.81051 StartY=6.6 StartZ=0 EndX=-7.62102 EndY=0 EndZ=0
    g4: LineSegment StartX=-7.62102 StartY=0 StartZ=0 EndX=-3.81051 EndY=-6.6 EndZ=0
    g5: LineSegment StartX=-3.81051 StartY=-6.6 StartZ=0 EndX=3.81051 EndY=-6.6 EndZ=0
    g6: Circle CenterX=0 CenterY=0 CenterZ=0 NormalX=0 NormalY=0 NormalZ=1 AngleXU=0 Radius=7.62102
    g7: LineSegment StartX=-3.81051 StartY=6.6 StartZ=0 EndX=3.81051 EndY=-6.6 EndZ=0
    g8: LineSegment StartX=3.81051 StartY=6.6 StartZ=0 EndX=-3.81051 EndY=-6.6 EndZ=0
  constraints (20):
    c: Coincident(g0,g1)
    c: Coincident(g1,g2)
    c: Coincident(g2,g3)
    c: Coincident(g3,g4)
    c: Coincident(g4,g5)
    c: Coincident(g5,g0)
    c: Equal(g0, g1-g5) x5
    c: PointOnObject(g0,g6)
    c: PointOnObject(g1,g6)
    c: PointOnObject(g2,g6)
    c: PointOnObject(g3,g6)
    c: PointOnObject(g4,g6)
    c: PointOnObject(g5,g6)
    c: Coincident(g6,g-1)
    c: PointOnObject(g0,g-1)
    c: Coincident(g7,g2)
    c: Coincident(g7,g0)
    c: Coincident(g8,g1)
    c: Coincident(g8,g4)
    c: DistanceY(g8,g8) = 13.2
FEATURE [PartDesign::Pocket] Pocket045  label="AzimuthBase_Nut"
  BaseFeature = -> Cylinder006
  Direction = (0,0,-1)
  Length = 8
  Length2 = 100
  Placement = pos=(0,0,-19.05) rot=(0,0,1;0rad)
  Profile = -> Sketch105
  Type = 0
FEATURE [Sketcher::SketchObject] Sketch106  label="AzimuthBase_Shaft_Sketch"
  FullyConstrained = true
  MapMode = 5
  Placement = pos=(0,0,-8) rot=(0,0,1;0rad)
  Support = -> [Pocket045]
  sketch-geometry (1):
    g0: Circle CenterX=0 CenterY=0 CenterZ=0 NormalX=0 NormalY=0 NormalZ=1 AngleXU=0 Radius=4.4
  constraints (2):
    c: Coincident(g0,g-1)
    c: Diameter(g0) = 8.8
FEATURE [PartDesign::Hole] Hole037  label="AzimuthBase_Shaft"
  BaseFeature = -> Pocket045
  CustomThreadClearance = 0
  Depth = 25
  DepthType = 1
  Diameter = 8.4
  DrillForDepth = false
  DrillPoint = 1
  DrillPointAngle = 118
  HoleCutCountersinkAngle = 90
  HoleCutCustomValues = false
  HoleCutDepth = 0
  HoleCutDiameter = 6.1
  HoleCutType = 0
  ModelThread = false
  Placement = pos=(0,0,-19.05) rot=(0,0,1;0rad)
  Profile = -> Sketch106
  Tapered = false
  TaperedAngle = 90
  ThreadClass = 0
  ThreadDepth = 23.5
  ThreadDepthType = 0
  ThreadDirection = 0
  ThreadFit = 1
  ThreadSize = 16
  ThreadType = 1
  Threaded = false
  UseCustomThreadClearance = false
FEATURE [PartDesign::CoordinateSystem] Local_CS207  label="LCS_AzimuthBase_Nut"
  AttacherType = Attacher::AttachEngine3D
  MapMode = 11
  Placement = pos=(0,0,-8) rot=(0,0,1;1.5708rad)
  Support = -> [Hole037]
FEATURE [PartDesign::CoordinateSystem] Local_CS208  label="LCS_AzimuthBase_Top"
  AttacherType = Attacher::AttachEngine3D
  MapMode = 11
  Placement = pos=(0,0,-19.05) rot=(0.707107,-0.707107,0;3.14159rad)
  Support = -> [Hole037]
FEATURE [PartDesign::Body] Body022020  label="AzimuthBase"
  Group = -> [Cylinder006,Sketch105,Pocket045,Sketch106,Hole037,Local_CS207,Local_CS208]
  Origin = -> Origin073
  Placement = pos=(0,0,-147) rot=(0,0,1;0rad)
  Tip = -> Hole037
  expr: .Placement.Base.z = <<Common>>#<<Parameters>>.datum_azbase - 15
COMPONENT P6 — recipe-attached ("TopRetainer", modeled in this document).
Construction recipe (the document's own serialized feature program — sketch geometry with constraints, then the solid features built on it; lengths are millimeters unless a unit is written):

FEATURE [Sketcher::SketchObject] Sketch107  label="TopRetainer_Shaft_Sketch"
  AttachmentOffset = pos=(0,0,13) rot=(0,0,1;0rad)
  FullyConstrained = true
  MapMode = 5
  Placement = pos=(13,-2.9e-15,2.9e-15) rot=(0.57735,0.57735,0.57735;2.0944rad)
  Support = -> [YZ_Plane075]
  expr: .AttachmentOffset.Base.z = 10 + <<Common>>#<<Parameters>>.sec_fthick
  sketch-geometry (1):
    g0: Circle CenterX=0 CenterY=0 CenterZ=0 NormalX=0 NormalY=0 NormalZ=1 AngleXU=0 Radius=2.75
  constraints (2):
    c: Coincident(g0,g-1)
    c: Diameter(g0) = 5.5
FEATURE [Sketcher::SketchObject] Sketch108  label="TopRetainer_BaseProfile"
  FullyConstrained = true
  MapMode = 5
  Support = -> [XY_Plane075]
  expr: Constraints[7] = 10 + <<Common>>#<<Parameters>>.alt_sideclamp + <<Common>>#<<Parameters>>.rocker_plate + <<Common>>#<<Parameters>>.rail_width - 1
  sketch-geometry (7):
    g0: LineSegment StartX=-32 StartY=12.4 StartZ=0 EndX=12.4 EndY=12.4 EndZ=0
    g1: LineSegment StartX=12.4 StartY=12.4 StartZ=0 EndX=12.4 EndY=-12.4 EndZ=0
    g2: LineSegment StartX=12.4 StartY=-12.4 StartZ=0 EndX=-32 EndY=-12.4 EndZ=0
    g3: LineSegment StartX=-32 StartY=-12.4 StartZ=0 EndX=-32 EndY=12.4 EndZ=0
    g4: GeomPoint X=12.4 Y=12.4 Z=0
    g5: GeomPoint X=12.4 Y=-12.4 Z=0
    g6: Circle CenterX=0 CenterY=0 CenterZ=0 NormalX=0 NormalY=0 NormalZ=1 AngleXU=0 Radius=3
  constraints (17):
    c: Coincident(g2,g3)
    c: Coincident(g3,g0)
    c: Horizontal(g0)
    c: Horizontal(g2)
    c: Vertical(g3)
    c: DistanceY(g4) = 12.4
    c: Symmetric(g4,g5,g-1)
    c: DistanceX(g0,g-1) = 32
    c: PointOnObject(g4,g0)
    c: PointOnObject(g4,g1)
    c: PointOnObject(g5,g1)
    c: PointOnObject(g5,g2)
    c: Coincident(g0,g1)
    c: Coincident(g2,g1)
    c: DistanceX(g0) = 12.4
    c: Coincident(g6,g-1)
    c: Diameter(g6) = 6
FEATURE [PartDesign::Pad] Pad039  label="TopRetainer_Base"
  Direction = (0,0,1)
  Length = 12
  Length2 = 5
  Midplane = true
  Profile = -> Sketch108
  Type = 4
FEATURE [PartDesign::Plane] DatumPlane028  label="DatumPlane_TopRetainer_RailSide"
  AttachmentOffset = pos=(0,0,32) rot=(0,0,1;0rad)
  Length = 60
  MapMode = 5
  Placement = pos=(-32,7.1e-15,-7.1e-15) rot=(-0.57735,0.57735,0.57735;4.18879rad)
  ResizeMode = 0
  Support = -> [YZ_Plane075]
  Width = 60
  expr: .AttachmentOffset.Base.z = 10 + <<Common>>#<<Parameters>>.alt_sideclamp + <<Common>>#<<Parameters>>.rocker_plate + <<Common>>#<<Parameters>>.rail_width - 1
FEATURE [Sketcher::SketchObject] Sketch109  label="TopRetainer_ArcCut_Sketch"
  FullyConstrained = true
  MapMode = 5
  Placement = pos=(-32,7.1e-15,-7.1e-15) rot=(-0.57735,0.57735,0.57735;4.18879rad)
  Support = -> [DatumPlane028]
  expr: Constraints[2] = <<Common>>#<<Parameters>>.rail_dia - <<Common>>#<<Parameters>>.rail_height * 2 - 1.5
  expr: Constraints[4] = <<Common>>#<<Parameters>>.rail_dia
  sketch-geometry (2):
    g0: Circle CenterX=0 CenterY=164.25 CenterZ=0 NormalX=0 NormalY=0 NormalZ=1 AngleXU=0 Radius=164.25
    g1: Circle CenterX=0 CenterY=164.25 CenterZ=0 NormalX=0 NormalY=0 NormalZ=1 AngleXU=0 Radius=200
  constraints (5):
    c: PointOnObject(g0,g-2)
    c: PointOnObject(g-1,g0)
    c: Diameter(g0) = 328.5
    c: Coincident(g1,g0)
    c: Diameter(g1) = 400
FEATURE [PartDesign::Plane] DatumPlane048  label="DatumPlane_TopRetainer_LowerSide"
  AttachmentOffset = pos=(0,0,10) rot=(0,0,1;0rad)
  Length = 67.6771
  MapMode = 5
  Placement = pos=(0,0,-10) rot=(0,1,0;3.14159rad)
  ResizeMode = 0
  Support = -> [XY_Plane075]
  Width = 60.6771
FEATURE [Sketcher::SketchObject] Sketch110  label="TopRetainer_PostCut_Sketch"
  FullyConstrained = true
  MapMode = 5
  Placement = pos=(0,0,-10) rot=(0,1,0;3.14159rad)
  Support = -> [DatumPlane048]
  sketch-geometry (24):
    g0: LineSegment StartX=-10.2 StartY=10.2 StartZ=0 EndX=-3 EndY=10.2 EndZ=0
    g1: LineSegment StartX=-3 StartY=10.2 StartZ=0 EndX=-3 EndY=8.2 EndZ=0
    g2: LineSegment StartX=-3 StartY=8.2 StartZ=0 EndX=3 EndY=8.2 EndZ=0
    g3: LineSegment StartX=3 StartY=8.2 StartZ=0 EndX=3 EndY=10.2 EndZ=0
    g4: LineSegment StartX=3 StartY=10.2 StartZ=0 EndX=10.2 EndY=10.2 EndZ=0
    g5: LineSegment StartX=10.2 StartY=10.2 StartZ=0 EndX=10.2 EndY=3 EndZ=0
    g6: LineSegment StartX=10.2 StartY=3 StartZ=0 EndX=8.2 EndY=3 EndZ=0
    g7: LineSegment StartX=8.2 StartY=3 StartZ=0 EndX=8.2 EndY=-3 EndZ=0
    g8: LineSegment StartX=8.2 StartY=-3 StartZ=0 EndX=10.2 EndY=-3 EndZ=0
    g9: LineSegment StartX=10.2 StartY=-3 StartZ=0 EndX=10.2 EndY=-10.2 EndZ=0
    g10: LineSegment StartX=10.2 StartY=-10.2 StartZ=0 EndX=3 EndY=-10.2 EndZ=0
    g11: LineSegment StartX=3 StartY=-10.2 StartZ=0 EndX=3 EndY=-8.2 EndZ=0
    g12: LineSegment StartX=3 StartY=-8.2 StartZ=0 EndX=-3 EndY=-8.2 EndZ=0
    g13: LineSegment StartX=-3 StartY=-8.2 StartZ=0 EndX=-3 EndY=-10.2 EndZ=0
    g14: LineSegment StartX=-3 StartY=-10.2 StartZ=0 EndX=-10.2 EndY=-10.2 EndZ=0
    g15: LineSegment StartX=-10.2 StartY=-10.2 StartZ=0 EndX=-10.2 EndY=-3 EndZ=0
    g16: LineSegment StartX=-10.2 StartY=-3 StartZ=0 EndX=-9.2 EndY=-3 EndZ=0
    g17: LineSegment StartX=-9.2 StartY=-3 StartZ=0 EndX=-9.2 EndY=3 EndZ=0
    g18: LineSegment StartX=-9.2 StartY=3 StartZ=0 EndX=-10.2 EndY=3 EndZ=0
    g19: LineSegment StartX=-10.2 StartY=3 StartZ=0 EndX=-10.2 EndY=10.2 EndZ=0
    g20: LineSegment StartX=-10.2 StartY=10.2 StartZ=0 EndX=10.2 EndY=10.2 EndZ=0
    g21: LineSegment StartX=10.2 StartY=10.2 StartZ=0 EndX=10.2 EndY=-10.2 EndZ=0
    g22: LineSegment StartX=10.2 StartY=-10.2 StartZ=0 EndX=-10.2 EndY=-10.2 EndZ=0
    g23: LineSegment StartX=-10.2 StartY=-10.2 StartZ=0 EndX=-10.2 EndY=10.2 EndZ=0
  constraints (62):
    c: Horizontal(g0)
    c: Coincident(g1,g0)
    c: Coincident(g2,g1)
    c: Vertical(g5)
    c: Coincident(g6,g5)
    c: Coincident(g8,g7)
    c: Coincident(g9,g8)
    c: Coincident(g10,g9)
    c: Horizontal(g10)
    c: Coincident(g11,g10)
    c: Coincident(g12,g11)
    c: Coincident(g13,g12)
    c: Coincident(g14,g13)
    c: Horizontal(g14)
    c: Coincident(g15,g14)
    c: Vertical(g15)
    c: Coincident(g16,g15)
    c: Coincident(g19,g18)
    c: Coincident(g19,g0)
    c: Coincident(g3,g4)
    c: Coincident(g6,g7)
    c: Coincident(g16,g17)
    c: Vertical(g19)
    c: Vertical(g13)
    c: Vertical(g11)
    c: Vertical(g9)
    c: Vertical(g1)
    c: Vertical(g3)
    c: Horizontal(g4)
    c: Horizontal(g6)
    c: Horizontal(g18)
    c: Horizontal(g16)
    c: Horizontal(g8)
    c: Coincident(g18,g17)
    c: Equal(g17,g2)
    c: Equal(g2,g7)
    c: Equal(g7,g12)
    c: DistanceY(g7,g7) = 6
    c: Coincident(g20,g21)
    c: Coincident(g21,g22)
    c: Coincident(g22,g23)
    c: Coincident(g23,g20)
    c: Horizontal(g20)
    c: Vertical(g23)
    c: Symmetric(g22,g21,g-2)
    c: Symmetric(g20,g21,g-1)
    c: Equal(g21,g22)
    c: DistanceY(g21,g21) = 20.4
    c: Coincident(g0,g20)
    c: Coincident(g5,g4)
    c: Coincident(g5,g20)
    c: Coincident(g9,g21)
    c: Coincident(g14,g22)
    c: Equal(g11,g8)
    c: Coincident(g2,g3)
    c: DistanceY(g1,g1) = 2
    c: Symmetric(g16,g17,g-1)
    c: Symmetric(g6,g7,g-1)
    c: Symmetric(g1,g2,g-2)
    c: Symmetric(g12,g11,g-2)
    c: Equal(g1,g6)
    c: DistanceX(g18,g18) = 1
FEATURE [PartDesign::Pocket] Pocket131  label="TopRetainer_ArcCut"
  BaseFeature = -> Pad039
  Direction = (1,-4e-16,2e-16)
  Length = 19
  Length2 = 5
  Profile = -> Sketch109
  Type = 0
  expr: Length = <<Common>>#<<Parameters>>.alt_sideclamp + <<Common>>#<<Parameters>>.rocker_plate + <<Common>>#<<Parameters>>.rail_width - 1 - <<Common>>#<<Parameters>>.sec_fthick
FEATURE [PartDesign::Pocket] Pocket132  label="TopRetainer_PostCut"
  BaseFeature = -> Pocket131
  Direction = (0,0,1)
  Length = 20
  Length2 = 5
  Profile = -> Sketch110
  Type = 0
FEATURE [PartDesign::Pocket] Pocket133  label="TopRetainer_Shaft"
  BaseFeature = -> Pocket132
  Direction = (-1,2e-16,-3e-16)
  Length = 13
  Length2 = 5
  Profile = -> Sketch107
  Type = 0
  expr: Length = 10 + <<Common>>#<<Parameters>>.sec_fthick
FEATURE [PartDesign::Fillet] Fillet005  label="TopRetainer_Fillet"
  Base = -> Pocket133 [Edge1,Edge40,Edge8,Edge38,Edge6,Edge5,Edge37,Edge34,Edge4,Edge35,Edge7]
  BaseFeature = -> Pocket133
  Radius = 1.5
  SupportTransform = false
  UseAllEdges = false
  expr: Radius = 1.5
FEATURE [PartDesign::CoordinateSystem] Local_CS256  label="LCS_TopRetainer_Attachment"
  AttacherType = Attacher::AttachEngine3D
  MapMode = 5
  Support = -> [XY_Plane075]
FEATURE [PartDesign::Body] Body022022  label="TopRetainer"
  Group = -> [Sketch108,Pad039,Sketch109,Sketch107,Sketch110,DatumPlane028,DatumPlane048,Pocket131,Pocket132,Pocket133,Fillet005,Local_CS256]
  Origin = -> Origin075
  Placement = pos=(158,0,-82) rot=(0,0,1;0rad)
  Tip = -> Fillet005
  expr: .Placement.Base.x = <<Common>>#<<Parameters>>.bolt_x + <<Common>>#<<Parameters>>.rail_width + <<Common>>#<<Parameters>>.alt_sideclamp + 2 + <<Common>>#<<Parameters>>.rocker_plate + 20
  expr: .Placement.Base.z = <<Common>>#<<Parameters>>.datum_rocker_z - <<Common>>#<<Parameters>>.rail_dia / 2 + <<Common>>#<<Parameters>>.rail_height
COMPONENT P7 — recipe-attached ("FullRetainer", modeled in this document).
Construction recipe (the document's own serialized feature program — sketch geometry with constraints, then the solid features built on it; lengths are millimeters unless a unit is written):

FEATURE [Sketcher::SketchObject] Sketch201  label="FullRetainer_BaseProfile_Sketch"
  FullyConstrained = true
  MapMode = 5
  Placement = pos=(0,0,0) rot=(1,0,0;1.5708rad)
  Support = -> [XZ_Plane097]
  expr: Constraints[19] = <<Common>>#<<Parameters>>.datum_rocker_z - <<Common>>#<<Parameters>>.datum_azbase + 10 - <<Common>>#<<Parameters>>.rail_dia / 2 + <<Common>>#<<Parameters>>.rail_height
  expr: Constraints[22] = <<Common>>#<<Parameters>>.pri_tol
  expr: Constraints[45] = <<Common>>#<<Parameters>>.rail_width + 5
  expr: Constraints[48] = <<Common>>#<<Parameters>>.rail_height
  sketch-geometry (17):
    g0: LineSegment StartX=2 StartY=8.5 StartZ=0 EndX=25 EndY=8.5 EndZ=0
    g1: LineSegment StartX=25 StartY=8.5 StartZ=0 EndX=25 EndY=-60 EndZ=0
    g2: LineSegment StartX=25 StartY=-60 StartZ=0 EndX=0 EndY=-60 EndZ=0
    g3: LineSegment StartX=1.77462 StartY=-38.0127 StartZ=0 EndX=15.2254 EndY=-36.4873 EndZ=0
    g4: LineSegment StartX=15 StartY=0.5 StartZ=0 EndX=2 EndY=0.5 EndZ=0
    g5: LineSegment StartX=2 StartY=0.5 StartZ=0 EndX=2 EndY=8.5 EndZ=0
    g6: LineSegment StartX=0 StartY=-40 StartZ=0 EndX=0 EndY=-47 EndZ=0
    g7: LineSegment StartX=0 StartY=-47 StartZ=0 EndX=-3 EndY=-47 EndZ=0
    g8: LineSegment StartX=-3 StartY=-47 StartZ=0 EndX=-3 EndY=-53 EndZ=0
    g9: LineSegment StartX=-3 StartY=-53 StartZ=0 EndX=0 EndY=-53 EndZ=0
    g10: LineSegment StartX=0 StartY=-53 StartZ=0 EndX=0 EndY=-60 EndZ=0
    g11: LineSegment StartX=17 StartY=-1.5 StartZ=0 EndX=17 EndY=-34.5 EndZ=0
    g12: ArcOfCircle CenterX=15 CenterY=-1.5 CenterZ=0 NormalX=0 NormalY=0 NormalZ=1 AngleXU=0 Radius=2 StartAngle=0 EndAngle=1.5708
    g13: LineSegment StartX=15 StartY=-1.5 StartZ=0 EndX=15 EndY=0.5 EndZ=0
    g14: LineSegment StartX=15 StartY=-1.5 StartZ=0 EndX=17 EndY=-1.5 EndZ=0
    g15: ArcOfCircle CenterX=2 CenterY=-40 CenterZ=0 NormalX=0 NormalY=0 NormalZ=1 AngleXU=0 Radius=2 StartAngle=1.68373 EndAngle=3.14159
    g16: ArcOfCircle CenterX=15 CenterY=-34.5 CenterZ=0 NormalX=0 NormalY=0 NormalZ=1 AngleXU=0 Radius=2 StartAngle=4.82532 EndAngle=6.28319
  constraints (49):
    c: Horizontal(g0)
    c: Coincident(g1,g0)
    c: Vertical(g1)
    c: Coincident(g2,g1)
    c: Horizontal(g2)
    c: Coincident(g5,g0)
    c: Coincident(g5,g4)
    c: Vertical(g5)
    c: Horizontal(g4)
    c: Horizontal(g7)
    c: Coincident(g8,g7)
    c: Vertical(g8)
    c: Coincident(g9,g8)
    c: Horizontal(g9)
    c: Coincident(g10,g9)
    c: Coincident(g10,g2)
    c: DistanceY(g8,g8) = 6
    c: DistanceX(g9,g9) = 3
    c: DistanceY(g2,g9) = 7
    c: DistanceY(g1,g-1) = 60
    c: Coincident(g6,g7)
    c: Vertical(g11)
    c: DistanceY(g-1,g4) = 0.5
    c: DistanceY(g5,g5) = 8
    c: DistanceX(g2,g1) = 25
    c: Vertical(g10)
    c: PointOnObject(g6,g10)
    c: Vertical(g6)
    c: PointOnObject(g2,g-2)
    c: Coincident(g12,g4)
    c: Coincident(g12,g11)
    c: Coincident(g13,g12)
    c: Coincident(g13,g4)
    c: Coincident(g14,g12)
    c: Coincident(g14,g11)
    c: Horizontal(g14)
    c: Vertical(g13)
    c: DistanceX(g-1,g4) = 2
    c: Tangent(g6,g15) = -1.5708
    c: Tangent(g3,g15) = 1.5708
    c: Tangent(g3,g16) = -1.5708
    c: Tangent(g11,g16) = 1.5708
    c: DistanceY(g2,g6) = 20
    c: Equal(g15,g16)
    c: Equal(g16,g12)
    c: DistanceX(g4) = 15
    c: DistanceX(g11,g0) = 8
    c: Radius(g12) = 2
    c: DistanceY(g11,g4) = 35
FEATURE [PartDesign::Pad] Pad053  label="FullRetainer_Base"
  Direction = (0,-1,-2e-16)
  Length = 20
  Length2 = 10
  Midplane = true
  Placement = pos=(0,0,0) rot=(1,0,0;1.5708rad)
  Profile = -> Sketch201
  Type = 0
FEATURE [Sketcher::SketchObject] Sketch203  label="FullRetainer_Shaft_Sketch"
  FullyConstrained = true
  MapMode = 5
  Placement = pos=(0,0,0) rot=(0.57735,0.57735,0.57735;2.0944rad)
  Support = -> [YZ_Plane097]
  expr: Constraints[2] = <<Common>>#<<Parameters>>.datum_rocker_z - <<Common>>#<<Parameters>>.datum_azbase + 10 - <<Common>>#<<Parameters>>.rail_dia / 2 + <<Common>>#<<Parameters>>.rail_height - 10
  sketch-geometry (1):
    g0: Circle CenterX=0 CenterY=-50 CenterZ=0 NormalX=0 NormalY=0 NormalZ=1 AngleXU=0 Radius=2.75
  constraints (3):
    c: PointOnObject(g0,g-2)
    c: Diameter(g0) = 5.5
    c: DistanceY(g0,g-1) = 50
FEATURE [Sketcher::SketchObject] Sketch204  label="FullRetainer_ArcCut_Sketch"
  ExternalGeometry = -> [Sketch201]
  FullyConstrained = true
  MapMode = 5
  Placement = pos=(0,0,0) rot=(1,0,0;1.5708rad)
  Support = -> [XZ_Plane097]
  sketch-geometry (5):
    g0: LineSegment StartX=0 StartY=0.5 StartZ=0 EndX=0 EndY=-34.5 EndZ=0
    g1: LineSegment StartX=0 StartY=-34.5 StartZ=0 EndX=17 EndY=-34.5 EndZ=0
    g2: ArcOfCircle CenterX=15 CenterY=-1.5 CenterZ=0 NormalX=0 NormalY=0 NormalZ=1 AngleXU=0 Radius=2 StartAngle=0 EndAngle=1.5708
    g3: LineSegment StartX=0 StartY=0.5 StartZ=0 EndX=15 EndY=0.5 EndZ=0
    g4: LineSegment StartX=17 StartY=-1.5 StartZ=0 EndX=17 EndY=-34.5 EndZ=0
  constraints (13):
    c: Vertical(g0)
    c: Coincident(g1,g0)
    c: Horizontal(g1)
    c: Coincident(g3,g0)
    c: Coincident(g3,g2)
    c: Coincident(g4,g2)
    c: Coincident(g4,g1)
    c: Coincident(g2,g-5)
    c: Coincident(g2,g-5)
    c: Equal(g2,g-5)
    c: PointOnObject(g0,g-2)
    c: Horizontal(g3)
    c: Coincident(g1,g-4)
FEATURE [PartDesign::Line] DatumLine  label="DatumLine_FullRetainer_Pivot"
  AttacherType = Attacher::AttachEngineLine
  AttachmentOffset = pos=(0,165.5,0) rot=(0,0,1;0rad)
  Length = 20
  MapMode = 29
  Placement = pos=(0,0,165.5) rot=(0.57735,0.57735,0.57735;2.0944rad)
  ResizeMode = 0
  Support = -> [X_Axis097]
  expr: .AttachmentOffset.Base.y = <<Common>>#<<Parameters>>.rail_dia / 2 - <<Common>>#<<Parameters>>.rail_height + <<Common>>#<<Parameters>>.pri_tol
FEATURE [PartDesign::Groove] Groove  label="FUllRetainer_ArcCut"
  Angle = 360
  Axis = (1,0,0)
  Base = (0,0,165.5)
  BaseFeature = -> Pad053
  Placement = pos=(0,0,0) rot=(1,0,0;1.5708rad)
  Profile = -> Sketch204
  ReferenceAxis = -> DatumLine
FEATURE [PartDesign::Pocket] Pocket190  label="FullRetainer_Shaft"
  BaseFeature = -> Groove
  Direction = (-1,2e-16,-3e-16)
  Length = 5
  Length2 = 5
  Midplane = true
  Placement = pos=(0,0,0) rot=(1,0,0;1.5708rad)
  Profile = -> Sketch203
  ReferenceAxis = -> Sketch203 [N_Axis]
  Type = 1
FEATURE [Sketcher::SketchObject] Sketch331  label="FullRetainer_Notch_Sketch"
  FullyConstrained = true
  MapMode = 5
  Support = -> [XY_Plane096]
  sketch-geometry (4):
    g0: LineSegment StartX=-6 StartY=5 StartZ=0 EndX=0 EndY=5 EndZ=0
    g1: LineSegment StartX=0 StartY=5 StartZ=0 EndX=0 EndY=-5 EndZ=0
    g2: LineSegment StartX=0 StartY=-5 StartZ=0 EndX=-6 EndY=-5 EndZ=0
    g3: LineSegment StartX=-6 StartY=-5 StartZ=0 EndX=-6 EndY=5 EndZ=0
  constraints (11):
    c: Coincident(g0,g1)
    c: Coincident(g1,g2)
    c: Coincident(g2,g3)
    c: Coincident(g3,g0)
    c: Horizontal(g0)
    c: Horizontal(g2)
    c: Vertical(g3)
    c: PointOnObject(g1,g-2)
    c: Symmetric(g1,g0,g-1)
    c: DistanceY(g3,g3) = 10
    c: DistanceX(g0,g0) = 6
FEATURE [PartDesign::Pocket] Pocket191  label="FullRetainer_Notch"
  BaseFeature = -> Pocket190
  Direction = (0,0,-1)
  Length = 5
  Length2 = 5
  Midplane = true
  Placement = pos=(0,0,0) rot=(1,0,0;1.5708rad)
  Profile = -> Sketch331
  ReferenceAxis = -> Sketch331 [N_Axis]
  Type = 1
FEATURE [PartDesign::Plane] DatumPlane  label="DatumPlane_FullRetainer_Outer"
  Length = 246.737
  MapMode = 11
  Placement = pos=(25,-3.91e-14,-50) rot=(0.707107,0,0.707107;3.14159rad)
  ResizeMode = 0
  Support = -> [Pocket191]
  Width = 71.2368
FEATURE [Sketcher::SketchObject] Sketch259  label="FullRetainer_CounterBore_Sketch"
  FullyConstrained = true
  MapMode = 5
  Placement = pos=(25,-3.91e-14,-50) rot=(0.707107,0,0.707107;3.14159rad)
  Support = -> [DatumPlane]
  sketch-geometry (1):
    g0: Circle CenterX=0 CenterY=0 CenterZ=0 NormalX=0 NormalY=0 NormalZ=1 AngleXU=0 Radius=5
  constraints (2):
    c: Diameter(g0) = 10
    c: Coincident(g0,g-1)
FEATURE [Sketcher::SketchObject] Sketch273  label="FullRetainer_CounterBore_Support_Sketch"
  ExternalGeometry = -> [Sketch259,Sketch203]
  FullyConstrained = true
  MapMode = 5
  Placement = pos=(25,-3.91e-14,-50) rot=(0.707107,0,0.707107;3.14159rad)
  Support = -> [DatumPlane]
  sketch-geometry (11):
    g0: LineSegment StartX=-2.24137 StartY=4.46948 StartZ=0 EndX=4.99137 EndY=0.293658 EndZ=0
    g1: LineSegment StartX=4.99137 StartY=-0.293658 StartZ=0 EndX=-2.24137 EndY=-4.46948 EndZ=0
    g2: LineSegment StartX=-2.75 StartY=-4.17582 StartZ=0 EndX=-2.75 EndY=4.17582 EndZ=0
    g3: ArcOfCircle CenterX=0 CenterY=2e-16 CenterZ=0 NormalX=0 NormalY=0 NormalZ=1 AngleXU=0 Radius=5 StartAngle=6.22442 EndAngle=6.34195
    g4: ArcOfCircle CenterX=0 CenterY=2e-16 CenterZ=0 NormalX=0 NormalY=0 NormalZ=1 AngleXU=0 Radius=5 StartAngle=4.13002 EndAngle=4.24756
    g5: ArcOfCircle CenterX=0 CenterY=2e-16 CenterZ=0 NormalX=0 NormalY=0 NormalZ=1 AngleXU=0 Radius=5 StartAngle=2.03563 EndAngle=2.15316
    g6: LineSegment StartX=0 StartY=2e-16 StartZ=0 EndX=1.375 EndY=2.38157 EndZ=0
    g7: LineSegment StartX=0 StartY=2e-16 StartZ=0 EndX=1.375 EndY=-2.38157 EndZ=0
    g8: GeomPoint X=-2.75 Y=0 Z=0
    g9: LineSegment StartX=1.375 StartY=2.38157 StartZ=0 EndX=-2.75 EndY=0 EndZ=0
    g10: LineSegment StartX=1.375 StartY=2.38157 StartZ=0 EndX=1.375 EndY=-2.38157 EndZ=0
  constraints (30):
    c: PointOnObject(g0,g-3)
    c: PointOnObject(g1,g-3)
    c: PointOnObject(g2,g-3)
    c: Coincident(g3,g-4)
    c: Coincident(g3,g1)
    c: Coincident(g3,g0)
    c: Coincident(g4,g3)
    c: Coincident(g4,g1)
    c: Coincident(g4,g2)
    c: Coincident(g5,g3)
    c: Coincident(g5,g2)
    c: Coincident(g5,g0)
    c: Vertical(g2)
    c: Coincident(g6,g3)
    c: Coincident(g7,g3)
    c: Equal(g1,g2)
    c: Equal(g2,g0)
    c: Perpendicular(g1,g7)
    c: Perpendicular(g0,g6)
    c: PointOnObject(g8,g2)
    c: PointOnObject(g8,g-4)
    c: PointOnObject(g8,g-1)
    c: Coincident(g9,g6)
    c: Coincident(g9,g8)
    c: Coincident(g10,g6)
    c: Coincident(g10,g7)
    c: Vertical(g10)
    c: Equal(g10,g9)
    c: PointOnObject(g7,g-4)
    c: PointOnObject(g6,g-4)
FEATURE [PartDesign::Pocket] Pocket192  label="FullRetainer_CounterBore"
  BaseFeature = -> Pocket191
  Direction = (-1,2e-16,-2e-16)
  Length = 10
  Length2 = 5
  Placement = pos=(0,0,0) rot=(1,0,0;1.5708rad)
  Profile = -> Sketch259
  ReferenceAxis = -> Sketch259 [N_Axis]
  Type = 0
FEATURE [PartDesign::Pocket] Pocket193  label="FullRetainer_CounterBore_Support"
  BaseFeature = -> Pocket192
  Direction = (-1,2e-16,-2e-16)
  Length = 10.2
  Length2 = 5
  Placement = pos=(0,0,0) rot=(1,0,0;1.5708rad)
  Profile = -> Sketch273
  ReferenceAxis = -> Sketch273 [N_Axis]
  Type = 0
FEATURE [PartDesign::Chamfer] Chamfer002
  Angle = 45
  Base = -> Pocket193 [Face21]
  BaseFeature = -> Pocket193
  ChamferType = 0
  FlipDirection = false
  Placement = pos=(0,0,0) rot=(1,0,0;1.5708rad)
  Size = 1
  Size2 = 1
  SupportTransform = false
  UseAllEdges = false
FEATURE [PartDesign::Fillet] Fillet013
  Base = -> Chamfer002 [Face7,Face5]
  BaseFeature = -> Chamfer002
  Placement = pos=(0,0,0) rot=(1,0,0;1.5708rad)
  Radius = 1
  SupportTransform = false
  UseAllEdges = false
FEATURE [PartDesign::Body] Body022044  label="FullRetainer"
  Group = -> [Sketch201,Pad053,Sketch203,Sketch204,DatumLine,Sketch259,Sketch273,Groove,Pocket190,Sketch331,Pocket191,DatumPlane,Pocket192,Pocket193,Chamfer002,Fillet013]
  Origin = -> Origin097
  Placement = pos=(123,0,-82) rot=(0,0,1;0rad)
  Tip = -> Fillet013
  expr: .Placement.Base.x = <<Common>>#<<Parameters>>.boxsize_x / 2
  expr: .Placement.Base.z = <<Common>>#<<Parameters>>.datum_rocker_z - <<Common>>#<<Parameters>>.rail_dia / 2 + <<Common>>#<<Parameters>>.rail_height
COMPONENT P8 — recipe-attached ("FullRetainerNoKnob", modeled in this document).
Construction recipe (the document's own serialized feature program — sketch geometry with constraints, then the solid features built on it; lengths are millimeters unless a unit is written):

FEATURE [Sketcher::SketchObject] Sketch256  label="FullRetainerNoKnob_BaseProfile_Sketch"
  FullyConstrained = true
  MapMode = 5
  Placement = pos=(0,0,0) rot=(1,0,0;1.5708rad)
  Support = -> [XZ_Plane110]
  expr: Constraints[24] = <<Common>>#<<Parameters>>.rocker_plate
  expr: Constraints[26] = <<Common>>#<<Parameters>>.datum_rocker_z - <<Common>>#<<Parameters>>.datum_azbase + 15 - <<Common>>#<<Parameters>>.rail_dia / 2 + <<Common>>#<<Parameters>>.rail_height
  expr: Constraints[27] = <<Common>>#<<Parameters>>.rocker_plate + <<Common>>#<<Parameters>>.rail_width
  expr: Constraints[29] = <<Common>>#<<Parameters>>.rail_height - 5
  expr: Constraints[30] = <<Common>>#<<Parameters>>.rail_dia / 2 - <<Common>>#<<Parameters>>.rail_height - sqrt((<<Common>>#<<Parameters>>.datum_rocker_z - <<Common>>#<<Parameters>>.datum_lowercell) ^ 2 + <<Common>>#<<Parameters>>.bolt_y ^ 2) - 10
  expr: Constraints[36] = <<Common>>#<<Parameters>>.pri_tol
  sketch-geometry (13):
    g0: LineSegment StartX=-12 StartY=8.5 StartZ=0 EndX=9 EndY=8.5 EndZ=0
    g1: LineSegment StartX=9 StartY=8.5 StartZ=0 EndX=9 EndY=-65 EndZ=0
    g2: LineSegment StartX=9 StartY=-65 StartZ=0 EndX=0 EndY=-65 EndZ=0
    g3: LineSegment StartX=0 StartY=-30 StartZ=0 EndX=2 EndY=-28.8314 EndZ=0
    g4: LineSegment StartX=-2 StartY=0.5 StartZ=0 EndX=-12 EndY=0.5 EndZ=0
    g5: LineSegment StartX=-12 StartY=0.5 StartZ=0 EndX=-12 EndY=8.5 EndZ=0
    g6: LineSegment StartX=0 StartY=-30 StartZ=0 EndX=0 EndY=-52 EndZ=0
    g7: LineSegment StartX=0 StartY=-52 StartZ=0 EndX=-2 EndY=-52 EndZ=0
    g8: LineSegment StartX=-2 StartY=-52 StartZ=0 EndX=-2 EndY=-58 EndZ=0
    g9: LineSegment StartX=-2 StartY=-58 StartZ=0 EndX=0 EndY=-58 EndZ=0
    g10: LineSegment StartX=0 StartY=-58 StartZ=0 EndX=0 EndY=-65 EndZ=0
    g11: LineSegment StartX=-2 StartY=0.5 StartZ=0 EndX=2 EndY=-3.5 EndZ=0
    g12: LineSegment StartX=2 StartY=-3.5 StartZ=0 EndX=2 EndY=-28.8314 EndZ=0
  constraints (40):
    c: Horizontal(g0)
    c: Coincident(g1,g0)
    c: Vertical(g1)
    c: Coincident(g2,g1)
    c: PointOnObject(g2,g-2)
    c: Horizontal(g2)
    c: PointOnObject(g3,g-2)
    c: Coincident(g5,g0)
    c: Coincident(g5,g4)
    c: Vertical(g5)
    c: Horizontal(g4)
    c: DistanceX(g3,g3) = 2
    c: Coincident(g6,g3)
    c: PointOnObject(g6,g-2)
    c: Horizontal(g7)
    c: Coincident(g8,g7)
    c: Vertical(g8)
    c: Coincident(g9,g8)
    c: PointOnObject(g9,g-2)
    c: Horizontal(g9)
    c: Coincident(g10,g9)
    c: Coincident(g10,g2)
    c: DistanceX(g3,g1) = 7
    c: DistanceY(g8,g8) = 6
    c: DistanceX(g9,g9) = 2
    c: DistanceY(g2,g9) = 7
    c: DistanceY(g1,g-1) = 65
    c: DistanceX(g4,g-1) = 12
    c: Coincident(g6,g7)
    c: DistanceY(g3,g-1) = 30
    c: DistanceY(g3) = -28.8314
    c: Coincident(g11,g4)
    c: Coincident(g12,g11)
    c: Coincident(g12,g3)
    c: Vertical(g12)
    c: Angle(g11,g12) = 2.35619
    c: DistanceY(g-1,g4) = 0.5
    c: DistanceY(g5,g5) = 8
    c: DistanceX(g2,g1) = 9
    c: DistanceX(g4,g4) = 10
FEATURE [PartDesign::Pad] Pad063  label="FullRetainerNoKnob_Base"
  Direction = (0,-1,-2e-16)
  Length = 20
  Length2 = 10
  Midplane = true
  Placement = pos=(0,0,0) rot=(1,0,0;1.5708rad)
  Profile = -> Sketch256
  Type = 0
FEATURE [Sketcher::SketchObject] Sketch257  label="FullRetainerNoKnob_Shaft_Sketch"
  FullyConstrained = true
  MapMode = 5
  Placement = pos=(0,0,0) rot=(0.57735,0.57735,0.57735;2.0944rad)
  Support = -> [YZ_Plane110]
  expr: Constraints[2] = <<Common>>#<<Parameters>>.datum_rocker_z - <<Common>>#<<Parameters>>.datum_azbase + 15 - <<Common>>#<<Parameters>>.rail_dia / 2 + <<Common>>#<<Parameters>>.rail_height - 10
  sketch-geometry (1):
    g0: Circle CenterX=0 CenterY=-55 CenterZ=0 NormalX=0 NormalY=0 NormalZ=1 AngleXU=0 Radius=2.75
  constraints (3):
    c: PointOnObject(g0,g-2)
    c: Diameter(g0) = 5.5
    c: DistanceY(g0,g-1) = 55
FEATURE [Sketcher::SketchObject] Sketch258  label="FullRetainer_ArcCut_Sketch001"
  ExternalGeometry = -> [Pad063]
  FullyConstrained = true
  MapMode = 5
  Placement = pos=(0,0,0) rot=(1,0,0;1.5708rad)
  Support = -> [XZ_Plane110]
  sketch-geometry (6):
    g0: LineSegment StartX=-12 StartY=0.5 StartZ=0 EndX=-12 EndY=-8.5 EndZ=0
    g1: LineSegment StartX=-12 StartY=-8.5 StartZ=0 EndX=2 EndY=-8.5 EndZ=0
    g2: ArcOfCircle CenterX=-2 CenterY=-3.5 CenterZ=0 NormalX=0 NormalY=0 NormalZ=1 AngleXU=0 Radius=4 StartAngle=0 EndAngle=1.5708
    g3: LineSegment StartX=-12 StartY=0.5 StartZ=0 EndX=-2 EndY=0.5 EndZ=0
    g4: LineSegment StartX=2 StartY=-3.5 StartZ=0 EndX=2 EndY=-8.5 EndZ=0
    g5: LineSegment StartX=0 StartY=-3.5 StartZ=0 EndX=2 EndY=-3.5 EndZ=0
  constraints (16):
    c: Vertical(g0)
    c: Coincident(g1,g0)
    c: Horizontal(g1)
    c: Coincident(g3,g0)
    c: Coincident(g3,g2)
    c: Coincident(g0,g-3)
    c: Coincident(g2,g-3)
    c: Coincident(g2,g-4)
    c: Coincident(g4,g2)
    c: Coincident(g4,g1)
    c: PointOnObject(g1,g-4)
    c: PointOnObject(g5,g-2)
    c: Coincident(g5,g2)
    c: Horizontal(g5)
    c: PointOnObject(g2,g5)
    c: DistanceY(g4,g4) = 5
FEATURE [PartDesign::Line] DatumLine001  label="DatumLine_FullRetainerNoKnob_Pivot"
  AttacherType = Attacher::AttachEngineLine
  AttachmentOffset = pos=(0,165.5,0) rot=(0,0,1;0rad)
  Length = 20
  MapMode = 29
  Placement = pos=(0,0,165.5) rot=(0.57735,0.57735,0.57735;2.0944rad)
  ResizeMode = 0
  Support = -> [X_Axis110]
  expr: .AttachmentOffset.Base.y = <<Common>>#<<Parameters>>.rail_dia / 2 - <<Common>>#<<Parameters>>.rail_height + <<Common>>#<<Parameters>>.pri_tol
FEATURE [PartDesign::Groove] Groove007  label="FullRetainerNoKnob_ArcCut"
  Angle = 360
  Axis = (1,0,0)
  Base = (0,0,165.5)
  BaseFeature = -> Pad063
  Placement = pos=(0,0,0) rot=(1,0,0;1.5708rad)
  Profile = -> Sketch258
  ReferenceAxis = -> DatumLine001
  Reversed = true
FEATURE [PartDesign::Pocket] Pocket173  label="FullRetainerNoKnob_Shaft"
  BaseFeature = -> Groove007
  Direction = (-1,2e-16,-3e-16)
  Length = 5
  Length2 = 5
  Midplane = true
  Placement = pos=(0,0,0) rot=(1,0,0;1.5708rad)
  Profile = -> Sketch257
  Type = 1
FEATURE [PartDesign::Fillet] Fillet011  label="FullRetainerNoKnob_Fillet"
  Base = -> Pocket173 [Edge4,Edge5,Edge24,Edge22,Edge25,Edge21,Edge36,Edge53,Edge35,Edge20,Edge44]
  BaseFeature = -> Pocket173
  Placement = pos=(0,0,0) rot=(1,0,0;1.5708rad)
  Radius = 2.5
  SupportTransform = false
  UseAllEdges = false
  expr: Radius = <<Common>>#<<Parameters>>.pri_fillet
FEATURE [PartDesign::Body] Body022056  label="FullRetainerNoKnob"
  Group = -> [Sketch256,Pad063,Sketch257,Sketch258,DatumLine001,Groove007,Pocket173,Fillet011]
  Origin = -> Origin110
  Placement = pos=(137,0,-82) rot=(0,0,1;0rad)
  Tip = -> Fillet011
  expr: .Placement.Base.x = <<Common>>#<<Parameters>>.boxsize_x / 2 + <<Common>>#<<Parameters>>.rail_width + 2 + <<Common>>#<<Parameters>>.rocker_plate
  expr: .Placement.Base.z = <<Common>>#<<Parameters>>.datum_rocker_z - <<Common>>#<<Parameters>>.rail_dia / 2 + <<Common>>#<<Parameters>>.rail_height
COMPONENT P9 — recipe-attached ("SideGuard", modeled in this document).
Construction recipe (the document's own serialized feature program — sketch geometry with constraints, then the solid features built on it; lengths are millimeters unless a unit is written):

FEATURE [PartDesign::ShapeBinder] ShapeBinder013  label="SideGuard_ShapeBinder_Rocker"
  Support = -> [Binder]
  TraceSupport = false
FEATURE [Sketcher::SketchObject] Sketch275  label="SideGuard_Outline_Sketch"
  ExternalGeometry = -> [ShapeBinder013]
  FullyConstrained = true
  MapMode = 5
  Placement = pos=(0,0,0) rot=(0.57735,0.57735,0.57735;2.0944rad)
  Support = -> [YZ_Plane114]
  expr: Constraints[43] = <<Common>>#<<Parameters>>.rocker_zspace - 10
  sketch-geometry (17):
    g0: LineSegment StartX=123 StartY=-10 StartZ=0 EndX=123 EndY=58.52 EndZ=0
    g1: LineSegment StartX=73 StartY=-10 StartZ=0 EndX=73 EndY=10 EndZ=0
    g2: ArcOfCircle CenterX=0 CenterY=215 CenterZ=0 NormalX=0 NormalY=0 NormalZ=1 AngleXU=0 Radius=195 StartAngle=5.27592 EndAngle=5.36861
    g3: GeomPoint X=122.025 Y=56.5392 Z=0
    g4: LineSegment StartX=118.975 StartY=60.5007 StartZ=0 EndX=122.025 EndY=56.5392 EndZ=0
    g5: ArcOfCircle CenterX=120.5 CenterY=58.52 CenterZ=0 NormalX=0 NormalY=0 NormalZ=1 AngleXU=0 Radius=2.5 StartAngle=-9e-16 EndAngle=2.22702
    g6: Circle CenterX=113 CenterY=30 CenterZ=0 NormalX=0 NormalY=0 NormalZ=1 AngleXU=0 Radius=2.75
    g7: Circle CenterX=83 CenterY=0 CenterZ=0 NormalX=0 NormalY=0 NormalZ=1 AngleXU=0 Radius=2.75
    g8: Circle CenterX=113 CenterY=0 CenterZ=0 NormalX=0 NormalY=0 NormalZ=1 AngleXU=0 Radius=3.25
    g9: ArcOfCircle CenterX=73 CenterY=40 CenterZ=0 NormalX=0 NormalY=0 NormalZ=1 AngleXU=0 Radius=30 StartAngle=4.71239 EndAngle=6.28319
    g10: ArcOfCircle CenterX=105.5 CenterY=48.0389 CenterZ=0 NormalX=0 NormalY=0 NormalZ=1 AngleXU=0 Radius=2.5 StartAngle=2.13433 EndAngle=3.14159
    g11: LineSegment StartX=103 StartY=40 StartZ=0 EndX=103 EndY=48.0389 EndZ=0
    g12: LineSegment StartX=103 StartY=48.0389 StartZ=0 EndX=105.5 EndY=48.0389 EndZ=0
    g13: LineSegment StartX=73 StartY=40 StartZ=0 EndX=103 EndY=40 EndZ=0
    g14: LineSegment StartX=98 StartY=-10 StartZ=0 EndX=73 EndY=-10 EndZ=0
    g15: LineSegment StartX=123 StartY=-10 StartZ=0 EndX=103 EndY=-10 EndZ=0
    g16: LineSegment StartX=103 StartY=-10 StartZ=0 EndX=98 EndY=-10 EndZ=0
  constraints (45):
    c: Vertical(g0)
    c: Coincident(g15,g0)
    c: Coincident(g1,g14)
    c: Vertical(g1)
    c: Coincident(g2,g-3)
    c: DistanceX(g-6,g0) = 10
    c: PointOnObject(g3,g-3)
    c: Coincident(g4,g3)
    c: Perpendicular(g-3,g4)
    c: Distance(g4) = 5
    c: Tangent(g2,g5) = 1.5708
    c: Tangent(g0,g5) = -1.5708
    c: Coincident(g4,g2)
    c: Coincident(g6,g-5)
    c: PointOnObject(g7,g-1)
    c: Coincident(g8,g-6)
    c: Diameter(g8) = 6.5
    c: Diameter(g6) = 5.5
    c: Equal(g6,g7)
    c: DistanceX(g7,g8) = 30
    c: DistanceX(g14,g7) = 10
    c: Radius(g5) = 2.5
    c: DistanceY(g1,g1) = 20
    c: Coincident(g9,g1)
    c: Equal(g10,g5)
    c: Tangent(g10,g2) = 1.5708
    c: PointOnObject(g9,g1)
    c: Coincident(g11,g9)
    c: Vertical(g11)
    c: Coincident(g11,g10)
    c: Coincident(g12,g10)
    c: Coincident(g12,g10)
    c: Horizontal(g12)
    c: Coincident(g13,g9)
    c: Coincident(g13,g9)
    c: Horizontal(g13)
    c: DistanceX(g10,g0) = 20
    c: Coincident(g16,g14)
    c: Horizontal(g14)
    c: Coincident(g15,g16)
    c: Horizontal(g15)
    c: DistanceY(g7,g1) = 10
    c: DistanceX(g15,g15) = 20
    c: Distance(g14,g15) = 5
    c: Horizontal(g16)
FEATURE [PartDesign::Pad] Pad067  label="SideGuard_Body"
  Direction = (1,-2e-16,3e-16)
  Length = 2.4
  Length2 = 100
  Placement = pos=(0,0,0) rot=(0.57735,0.57735,0.57735;2.0944rad)
  Profile = -> Sketch275
  Type = 0
FEATURE [Sketcher::SketchObject] Sketch288  label="SideGuard_SideRail_Sketch"
  ExternalGeometry = -> [ShapeBinder013,Sketch275]
  FullyConstrained = true
  MapMode = 5
  Placement = pos=(0,0,0) rot=(-0.57735,0.57735,0.57735;4.18879rad)
  Support = -> [YZ_Plane114]
  sketch-geometry (10):
    g0: LineSegment StartX=-88 StartY=3 StartZ=0 EndX=-103 EndY=3 EndZ=0
    g1: LineSegment StartX=-103 StartY=3 StartZ=0 EndX=-103 EndY=-3 EndZ=0
    g2: LineSegment StartX=-103 StartY=-3 StartZ=0 EndX=-88 EndY=-3 EndZ=0
    g3: LineSegment StartX=-88 StartY=-3 StartZ=0 EndX=-88 EndY=3 EndZ=0
    g4: LineSegment StartX=-73 StartY=3 StartZ=0 EndX=-78 EndY=3 EndZ=0
    g5: LineSegment StartX=-78 StartY=3 StartZ=0 EndX=-78 EndY=-3 EndZ=0
    g6: LineSegment StartX=-78 StartY=-3 StartZ=0 EndX=-73 EndY=-3 EndZ=0
    g7: LineSegment StartX=-73 StartY=-3 StartZ=0 EndX=-73 EndY=3 EndZ=0
    g8: LineSegment StartX=-88 StartY=0 StartZ=0 EndX=-83 EndY=0 EndZ=0
    g9: LineSegment StartX=-83 StartY=0 StartZ=0 EndX=-78 EndY=0 EndZ=0
  constraints (30):
    c: Coincident(g0,g1)
    c: Coincident(g1,g2)
    c: Coincident(g2,g3)
    c: Coincident(g3,g0)
    c: Horizontal(g0)
    c: Horizontal(g2)
    c: Vertical(g1)
    c: Vertical(g3)
    c: Coincident(g4,g5)
    c: Coincident(g5,g6)
    c: Coincident(g6,g7)
    c: Coincident(g7,g4)
    c: Horizontal(g4)
    c: Horizontal(g6)
    c: Vertical(g5)
    c: Symmetric(g4,g6,g-1)
    c: DistanceY(g5,g5) = 6
    c: PointOnObject(g0,g4)
    c: PointOnObject(g2,g6)
    c: PointOnObject(g8,g3)
    c: Coincident(g9,g8)
    c: PointOnObject(g9,g5)
    c: Horizontal(g8)
    c: Horizontal(g9)
    c: Equal(g9,g8)
    c: DistanceX(g0,g4) = 10
    c: DistanceX(g-3,g8) = 30
    c: DistanceX(g-3,g0) = 10
    c: PointOnObject(g8,g-1)
    c: PointOnObject(g6,g-4)
FEATURE [PartDesign::Pad] Pad073  label="SideGuard_SideRail"
  BaseFeature = -> Pad067
  Direction = (-1,2e-16,-3e-16)
  Length = 3
  Length2 = 10
  Placement = pos=(0,0,0) rot=(0.57735,0.57735,0.57735;2.0944rad)
  Profile = -> Sketch288
  ReferenceAxis = -> Sketch288 [N_Axis]
  Type = 0
FEATURE [Sketcher::SketchObject] Sketch  label="SideGuard_Block_Sketch"
  ExternalGeometry = -> [ShapeBinder013]
  FullyConstrained = true
  MapMode = 5
  Placement = pos=(0,0,0) rot=(0.57735,0.57735,0.57735;2.0944rad)
  Support = -> [YZ_Plane114]
  expr: Constraints[3] = <<Common>>#<<Parameters>>.rocker_zspace
  expr: Constraints[8] = <<Common>>#<<Parameters>>.pri_fillet
  sketch-geometry (7):
    g0: LineSegment StartX=123 StartY=-15 StartZ=0 EndX=103 EndY=-15 EndZ=0
    g1: Circle CenterX=113 CenterY=0 CenterZ=0 NormalX=0 NormalY=0 NormalZ=1 AngleXU=0 Radius=3.25
    g2: ArcOfCircle CenterX=105.5 CenterY=42.1532 CenterZ=0 NormalX=0 NormalY=0 NormalZ=1 AngleXU=0 Radius=2.5 StartAngle=2.1188 EndAngle=3.14159
    g3: ArcOfCircle CenterX=120.5 CenterY=52.2548 CenterZ=0 NormalX=0 NormalY=0 NormalZ=1 AngleXU=0 Radius=2.5 StartAngle=-9e-16 EndAngle=2.20814
    g4: LineSegment StartX=123 StartY=52.2548 StartZ=0 EndX=123 EndY=-15 EndZ=0
    g5: LineSegment StartX=103 StartY=-15 StartZ=0 EndX=103 EndY=42.1532 EndZ=0
    g6: ArcOfCircle CenterX=0 CenterY=215 CenterZ=0 NormalX=0 NormalY=0 NormalZ=1 AngleXU=0 Radius=200 StartAngle=5.2604 EndAngle=5.34973
  constraints (17):
    c: Coincident(g0,g4)
    c: Symmetric(g4,g0,g-4)
    c: DistanceX(g0,g0) = 20
    c: DistanceY(g4,g-4) = 15
    c: Coincident(g1,g-4)
    c: Diameter(g1) = 6.5
    c: Coincident(g5,g0)
    c: Equal(g3,g2)
    c: Radius(g3) = 2.5
    c: Vertical(g4)
    c: Vertical(g5)
    c: Coincident(g6,g-3)
    c: PointOnObject(g6,g-3)
    c: Tangent(g5,g2) = 1.5708
    c: Tangent(g2,g6) = 1.5708
    c: Tangent(g3,g6) = 1.5708
    c: Tangent(g4,g3) = 1.5708
FEATURE [PartDesign::Line] DatumLine002  label="SideGuard_DatumLine_RockerPivot"
  AttacherType = Attacher::AttachEngineLine
  Length = 20
  MapMode = 19
  Placement = pos=(0,0,215) rot=(0.57735,0.57735,0.57735;2.0944rad)
  ResizeMode = 0
  Support = -> [ShapeBinder013]
FEATURE [Sketcher::SketchObject] Sketch307  label="SideGuard_SidePins_Sketch"
  AttachmentOffset = pos=(0,0,12) rot=(0,0,1;0rad)
  ExternalGeometry = -> [ShapeBinder013]
  FullyConstrained = true
  MapMode = 5
  Placement = pos=(-12,2.7e-15,-2.7e-15) rot=(-0.57735,0.57735,0.57735;4.18879rad)
  Support = -> [YZ_Plane114]
  expr: .AttachmentOffset.Base.z = <<Common>>#<<Parameters>>.rail_width + 2
  sketch-geometry (19):
    g0: LineSegment StartX=-116 StartY=10 StartZ=0 EndX=-110 EndY=10 EndZ=0
    g1: LineSegment StartX=-110 StartY=10 StartZ=0 EndX=-110 EndY=7 EndZ=0
    g2: LineSegment StartX=-110 StartY=7 StartZ=0 EndX=-116 EndY=7 EndZ=0
    g3: LineSegment StartX=-116 StartY=7 StartZ=0 EndX=-116 EndY=10 EndZ=0
    g4: LineSegment StartX=-123 StartY=3 StartZ=0 EndX=-120 EndY=3 EndZ=0
    g5: LineSegment StartX=-120 StartY=3 StartZ=0 EndX=-120 EndY=-3 EndZ=0
    g6: LineSegment StartX=-120 StartY=-3 StartZ=0 EndX=-123 EndY=-3 EndZ=0
    g7: LineSegment StartX=-123 StartY=-3 StartZ=0 EndX=-123 EndY=3 EndZ=0
    g8: LineSegment StartX=-106 StartY=3 StartZ=0 EndX=-103 EndY=3 EndZ=0
    g9: LineSegment StartX=-103 StartY=3 StartZ=0 EndX=-103 EndY=-3 EndZ=0
    g10: LineSegment StartX=-103 StartY=-3 StartZ=0 EndX=-106 EndY=-3 EndZ=0
    g11: LineSegment StartX=-106 StartY=-3 StartZ=0 EndX=-106 EndY=3 EndZ=0
    g12: LineSegment StartX=-116 StartY=-7 StartZ=0 EndX=-110 EndY=-7 EndZ=0
    g13: LineSegment StartX=-110 StartY=-7 StartZ=0 EndX=-110 EndY=-10 EndZ=0
    g14: LineSegment StartX=-110 StartY=-10 StartZ=0 EndX=-116 EndY=-10 EndZ=0
    g15: LineSegment StartX=-116 StartY=-10 StartZ=0 EndX=-116 EndY=-7 EndZ=0
    g16: LineSegment StartX=-113 StartY=10 StartZ=0 EndX=-113 EndY=-10 EndZ=0
    g17: LineSegment StartX=-120 StartY=3 StartZ=0 EndX=-106 EndY=3 EndZ=0
    g18: LineSegment StartX=-116 StartY=7 StartZ=0 EndX=-116 EndY=-7 EndZ=0
  constraints (52):
    c: Coincident(g0,g1)
    c: Coincident(g1,g2)
    c: Coincident(g2,g3)
    c: Coincident(g3,g0)
    c: Horizontal(g2)
    c: Vertical(g1)
    c: Vertical(g3)
    c: Coincident(g4,g5)
    c: Coincident(g5,g6)
    c: Coincident(g6,g7)
    c: Coincident(g7,g4)
    c: Horizontal(g4)
    c: Horizontal(g6)
    c: Vertical(g5)
    c: Coincident(g8,g9)
    c: Coincident(g9,g10)
    c: Coincident(g10,g11)
    c: Coincident(g11,g8)
    c: Horizontal(g8)
    c: Horizontal(g10)
    c: Vertical(g9)
    c: Vertical(g11)
    c: Coincident(g12,g13)
    c: Coincident(g13,g14)
    c: Coincident(g14,g15)
    c: Coincident(g15,g12)
    c: Horizontal(g12)
    c: Horizontal(g14)
    c: Vertical(g13)
    c: Vertical(g15)
    c: PointOnObject(g16,g0)
    c: PointOnObject(g16,g14)
    c: Vertical(g16)
    c: Symmetric(g4,g6,g-1)
    c: Symmetric(g0,g0,g16)
    c: Equal(g0,g7)
    c: Equal(g7,g14)
    c: Equal(g14,g9)
    c: Equal(g3,g6)
    c: Equal(g6,g13)
    c: Equal(g13,g8)
    c: DistanceX(g0,g0) = 6
    c: DistanceY(g3,g3) = 3
    c: Coincident(g17,g4)
    c: Coincident(g18,g2)
    c: Coincident(g18,g12)
    c: Coincident(g17,g8)
    c: PointOnObject(g-3,g16)
    c: Equal(g17,g18)
    c: Symmetric(g4,g8,g16)
    c: Symmetric(g2,g12,g-1)
    c: DistanceY(g14,g0) = 20
FEATURE [PartDesign::Body] Body022060  label="SideGuard"
  Group = -> [ShapeBinder013,Sketch275,Pad067,Sketch288,Pad073,Sketch,DatumLine002,Sketch307]
  Origin = -> Origin114
  Placement = pos=(135,0,-132) rot=(0,0,1;0rad)
  Tip = -> Pad073
  expr: .Placement.Base.x = <<Common>>#<<Parameters>>.boxsize_x / 2 + <<Common>>#<<Parameters>>.rail_width + 2
  expr: .Placement.Base.z = <<Common>>#<<Parameters>>.datum_azbase
COMPONENT P10 — recipe-attached ("BaseBlock", modeled in this document).
Construction recipe (the document's own serialized feature program — sketch geometry with constraints, then the solid features built on it; lengths are millimeters unless a unit is written):

FEATURE [Sketcher::SketchObject] Sketch290  label="BaseBlock_Base_Sketch"
  FullyConstrained = true
  MapMode = 5
  Support = -> [XY_Plane115]
  expr: Constraints[0] = <<Common>>#<<Parameters>>.bolt_y
  sketch-geometry (12):
    g0: GeomPoint X=-35.6826 Y=113 Z=0
    g1: LineSegment StartX=-27.2213 StartY=122 StartZ=0 EndX=27.2213 EndY=122 EndZ=0
    g2: LineSegment StartX=50.6826 StartY=114.264 StartZ=0 EndX=50.6826 EndY=106.626 EndZ=0
    g3: LineSegment StartX=-50.6826 StartY=106.626 StartZ=0 EndX=-50.6826 EndY=114.264 EndZ=0
    g4: Circle CenterX=-35.6826 CenterY=113 CenterZ=0 NormalX=0 NormalY=0 NormalZ=1 AngleXU=0 Radius=2.25
    g5: ArcOfCircle CenterX=0 CenterY=0 CenterZ=0 NormalX=0 NormalY=0 NormalZ=1 AngleXU=0 Radius=125 StartAngle=1.79033 EndAngle=1.98828
    g6: ArcOfCircle CenterX=0 CenterY=0 CenterZ=0 NormalX=0 NormalY=0 NormalZ=1 AngleXU=0 Radius=125 StartAngle=1.15331 EndAngle=1.35127
    g7: ArcOfCircle CenterX=-45.6826 CenterY=106.626 CenterZ=0 NormalX=0 NormalY=0 NormalZ=1 AngleXU=0 Radius=5 StartAngle=3.14159 EndAngle=5.11717
    g8: ArcOfCircle CenterX=45.6826 CenterY=106.626 CenterZ=0 NormalX=0 NormalY=0 NormalZ=1 AngleXU=0 Radius=5 StartAngle=4.30761 EndAngle=6.28319
    g9: LineSegment StartX=-50.6826 StartY=114.264 StartZ=0 EndX=50.6826 EndY=114.264 EndZ=0
    g10: ArcOfCircle CenterX=0 CenterY=0 CenterZ=0 NormalX=0 NormalY=0 NormalZ=1 AngleXU=0 Radius=111 StartAngle=1.16602 EndAngle=1.97558
    g11: LineSegment StartX=-45.6826 StartY=106.626 StartZ=0 EndX=-45.6826 EndY=101.626 EndZ=0
  constraints (30):
    c: DistanceY(g0) = 113
    c: Vertical(g2)
    c: Vertical(g3)
    c: Symmetric(g1,g1,g-2)
    c: Equal(g2,g3)
    c: Coincident(g4,g0)
    c: Diameter(g4) = 4.5
    c: Distance(g-1,g4) = 118.5
    c: DistanceX(g3,g4) = 15
    c: Coincident(g5,g-1)
    c: Coincident(g5,g3)
    c: Coincident(g6,g5)
    c: Coincident(g6,g2)
    c: Coincident(g5,g1)
    c: Coincident(g6,g1)
    c: DistanceY(g4,g1) = 9
    c: Diameter(g6) = 250
    c: Equal(g8,g7)
    c: Tangent(g8,g2) = 1.5708
    c: Tangent(g7,g3) = 1.5708
    c: Coincident(g9,g3)
    c: Coincident(g9,g2)
    c: Coincident(g10,g5)
    c: Tangent(g10,g7) = 1.5708
    c: Tangent(g10,g8) = 1.5708
    c: Radius(g10) = 111
    c: Coincident(g11,g7)
    c: PointOnObject(g11,g7)
    c: Vertical(g11)
    c: Radius(g7) = 5
FEATURE [PartDesign::Pad] Pad  label="BaseBlock_Base"
  Direction = (0,0,1)
  Length = 2
  Length2 = 10
  Profile = -> Sketch290
  ReferenceAxis = -> Sketch290 [N_Axis]
  Reversed = true
  Type = 0
FEATURE [Sketcher::SketchObject] Sketch291  label="BaseBlock_Tab_Sketch"
  ExternalGeometry = -> [Sketch290]
  FullyConstrained = true
  MapMode = 5
  Support = -> [XY_Plane115]
  sketch-geometry (17):
    g0: LineSegment StartX=-46.5725 StartY=116 StartZ=0 EndX=-40.6826 EndY=116 EndZ=0
    g1: LineSegment StartX=-40.6826 StartY=116 StartZ=0 EndX=-40.6826 EndY=110 EndZ=0
    g2: LineSegment StartX=-40.6826 StartY=110 StartZ=0 EndX=-50.6826 EndY=110 EndZ=0
    g3: LineSegment StartX=-50.6826 StartY=110 StartZ=0 EndX=-50.6826 EndY=114.264 EndZ=0
    g4: LineSegment StartX=46.5725 StartY=116 StartZ=0 EndX=-30.6826 EndY=116 EndZ=0
    g5: LineSegment StartX=-30.6826 StartY=116 StartZ=0 EndX=-30.6826 EndY=110 EndZ=0
    g6: LineSegment StartX=50.6826 StartY=110 StartZ=0 EndX=50.6826 EndY=114.264 EndZ=0
    g7: LineSegment StartX=-35.6826 StartY=113 StartZ=0 EndX=0 EndY=113 EndZ=0
    g8: LineSegment StartX=-40.6826 StartY=116 StartZ=0 EndX=-35.6826 EndY=116 EndZ=0
    g9: LineSegment StartX=-35.6826 StartY=116 StartZ=0 EndX=-30.6826 EndY=116 EndZ=0
    g10: LineSegment StartX=-35.6826 StartY=116 StartZ=0 EndX=-35.6826 EndY=113 EndZ=0
    g11: LineSegment StartX=-40.6826 StartY=110 StartZ=0 EndX=-30.6826 EndY=110 EndZ=0
    g12: ArcOfCircle CenterX=0 CenterY=0 CenterZ=0 NormalX=0 NormalY=0 NormalZ=1 AngleXU=0 Radius=125 StartAngle=1.95258 EndAngle=1.98828
    g13: ArcOfCircle CenterX=0 CenterY=0 CenterZ=0 NormalX=0 NormalY=0 NormalZ=1 AngleXU=0 Radius=125 StartAngle=1.15331 EndAngle=1.18901
    g14: LineSegment StartX=-30.6826 StartY=110 StartZ=0 EndX=-14.8661 EndY=110 EndZ=0
    g15: LineSegment StartX=14.8661 StartY=110 StartZ=0 EndX=50.6826 EndY=110 EndZ=0
    g16: ArcOfCircle CenterX=0 CenterY=0 CenterZ=0 NormalX=0 NormalY=0 NormalZ=1 AngleXU=0 Radius=111 StartAngle=1.43646 EndAngle=1.70513
  constraints (45):
    c: Coincident(g0,g1)
    c: Coincident(g1,g2)
    c: Coincident(g2,g3)
    c: Horizontal(g0)
    c: Horizontal(g2)
    c: Coincident(g4,g5)
    c: Coincident(g5,g14)
    c: Horizontal(g4)
    c: Equal(g1,g5)
    c: PointOnObject(g7,g-2)
    c: Horizontal(g7)
    c: Symmetric(g4,g5,g7)
    c: Vertical(g1)
    c: Coincident(g8,g0)
    c: Horizontal(g8)
    c: Coincident(g9,g8)
    c: Coincident(g9,g4)
    c: Coincident(g10,g8)
    c: Coincident(g10,g7)
    c: Vertical(g10)
    c: Equal(g8,g9)
    c: DistanceX(g0,g4) = 10
    c: Coincident(g11,g1)
    c: Coincident(g11,g5)
    c: Horizontal(g11)
    c: Coincident(g3,g12)
    c: Coincident(g12,g0)
    c: Coincident(g6,g13)
    c: Coincident(g4,g13)
    c: Coincident(g6,g-4)
    c: Vertical(g6)
    c: Vertical(g3)
    c: Coincident(g3,g-3)
    c: Coincident(g15,g6)
    c: Coincident(g7,g-5)
    c: DistanceY(g5,g5) = 6
    c: Coincident(g13,g12)
    c: Coincident(g12,g-1)
    c: Horizontal(g14)
    c: Horizontal(g15)
    c: Horizontal(g6,g5)
    c: Coincident(g16,g12)
    c: Coincident(g16,g14)
    c: Coincident(g16,g15)
    c: Radius(g16) = 111
FEATURE [PartDesign::Pad] Pad074  label="BaseBlock_Tab"
  BaseFeature = -> Pad
  Direction = (0,0,1)
  Length = 2.4
  Length2 = 10
  Profile = -> Sketch291
  ReferenceAxis = -> Sketch291 [N_Axis]
  Type = 0
FEATURE [PartDesign::Chamfer] Chamfer005  label="BaseBlock-Chamfer"
  Angle = 45
  Base = -> Pad074 [Face6,Face24,Face18]
  BaseFeature = -> Pad074
  ChamferType = 0
  FlipDirection = false
  Size = 0.4
  Size2 = 1
  SupportTransform = false
  UseAllEdges = false
FEATURE [PartDesign::CoordinateSystem] Local_CS268  label="LCS_BaseBlock_Slewbearing_Top"
  AttacherType = Attacher::AttachEngine3D
  AttachmentOffset = pos=(0,0,-2) rot=(0,0,1;0rad)
  MapMode = 5
  Placement = pos=(0,0,-2) rot=(0,0,1;0rad)
  Support = -> [XY_Plane115]
FEATURE [PartDesign::CoordinateSystem] Local_CS278  label="LCS_BaseBlock_TNut"
  AttacherType = Attacher::AttachEngine3D
  AttachmentOffset = pos=(0,0,0) rot=(0,0,1;1.5708rad)
  MapMode = 11
  Placement = pos=(-35.6826,113,0) rot=(0,-1,0;3.14159rad)
  Support = -> [Pad]
FEATURE [PartDesign::Body] Body022061  label="BaseBlock"
  Group = -> [Sketch290,Pad,Sketch291,Pad074,Chamfer005,Local_CS268,Local_CS278]
  Origin = -> Origin115
  Placement = pos=(0,0,-142) rot=(0,0,1;0rad)
  Tip = -> Chamfer005
  expr: .Placement.Base.z = <<Common>>#<<Parameters>>.datum_azbase - 10
COMPONENT P11 — recipe-attached ("BasePadCorner", modeled in this document).
Construction recipe (the document's own serialized feature program — sketch geometry with constraints, then the solid features built on it; lengths are millimeters unless a unit is written):

FEATURE [Sketcher::SketchObject] Sketch297  label="BasePad_Body_Sketch297"
  FullyConstrained = true
  MapMode = 5
  Support = -> [XY_Plane117]
  expr: Constraints[24] = <<Common>>#<<Parameters>>.pri_fillet
  sketch-geometry (15):
    g0: Circle CenterX=-73.5391 CenterY=73.5391 CenterZ=0 NormalX=0 NormalY=0 NormalZ=1 AngleXU=0 Radius=2.5
    g1: ArcOfCircle CenterX=-100.992 CenterY=100.992 CenterZ=0 NormalX=0 NormalY=0 NormalZ=1 AngleXU=0 Radius=1.25 StartAngle=1.5708 EndAngle=3.14159
    g2: LineSegment StartX=-100.992 StartY=102.242 StartZ=0 EndX=-61.9916 EndY=102.242 EndZ=0
    g3: ArcOfCircle CenterX=-61.9916 CenterY=100.992 CenterZ=0 NormalX=0 NormalY=0 NormalZ=1 AngleXU=0 Radius=1.25 StartAngle=-3.6e-15 EndAngle=1.5708
    g4: LineSegment StartX=-60.7416 StartY=100.992 StartZ=0 EndX=-60.7416 EndY=61.9916 EndZ=0
    g5: ArcOfCircle CenterX=-61.9916 CenterY=61.9916 CenterZ=0 NormalX=0 NormalY=0 NormalZ=1 AngleXU=0 Radius=1.25 StartAngle=4.71239 EndAngle=6.28319
    g6: LineSegment StartX=-61.9916 StartY=60.7416 StartZ=0 EndX=-100.992 EndY=60.7416 EndZ=0
    g7: ArcOfCircle CenterX=-100.992 CenterY=61.9916 CenterZ=0 NormalX=0 NormalY=0 NormalZ=1 AngleXU=0 Radius=1.25 StartAngle=3.14159 EndAngle=4.71239
    g8: LineSegment StartX=-102.242 StartY=61.9916 StartZ=0 EndX=-102.242 EndY=100.992 EndZ=0
    g9: GeomPoint X=-102.242 Y=102.242 Z=0
    g10: GeomPoint X=-60.7416 Y=60.7416 Z=0
    g11: LineSegment StartX=-73.5391 StartY=73.5391 StartZ=0 EndX=0 EndY=0 EndZ=0
    g12: Circle CenterX=-83.7922 CenterY=83.7922 CenterZ=0 NormalX=0 NormalY=0 NormalZ=1 AngleXU=0 Radius=2.5
    g13: ArcOfCircle CenterX=0 CenterY=0 CenterZ=0 NormalX=0 NormalY=0 NormalZ=1 AngleXU=0 Radius=118.5 StartAngle=2.12132 EndAngle=2.59107
    g14: Circle CenterX=-73.5391 CenterY=73.5391 CenterZ=0 NormalX=0 NormalY=0 NormalZ=1 AngleXU=0 Radius=1
  constraints (36):
    c: Distance(g-1,g0) = 104
    c: Diameter(g0) = 5
    c: Tangent(g1,g2) = 1.5708
    c: Tangent(g2,g3) = 1.5708
    c: Tangent(g3,g4) = 1.5708
    c: Tangent(g4,g5) = 1.5708
    c: Tangent(g5,g6) = 1.5708
    c: Tangent(g6,g7) = 1.5708
    c: Tangent(g7,g8) = 1.5708
    c: Tangent(g8,g1) = 1.5708
    c: Horizontal(g2)
    c: Horizontal(g6)
    c: Vertical(g4)
    c: Vertical(g8)
    c: Equal(g1,g3)
    c: Equal(g3,g5)
    c: Equal(g5,g7)
    c: PointOnObject(g9,g2)
    c: PointOnObject(g9,g8)
    c: PointOnObject(g10,g4)
    c: PointOnObject(g10,g6)
    c: Equal(g2,g8)
    c: Coincident(g11,g0)
    c: Angle(g11) = -0.785398
    c: Diameter(g3) = 2.5
    c: DistanceX(g2,g2) = 39
    c: Coincident(g11,g-1)
    c: Equal(g12,g0)
    c: PointOnObject(g12,g11)
    c: Distance(g12,g11) = 118.5
    c: Coincident(g13,g11)
    c: Coincident(g13,g7)
    c: Coincident(g13,g3)
    c: PointOnObject(g12,g13)
    c: Coincident(g14,g0)
    c: Diameter(g14) = 2
FEATURE [Sketcher::SketchObject] Sketch298  label="BasePad_Pillar_Sketch"
  ExternalGeometry = -> [Sketch297]
  FullyConstrained = true
  MapMode = 5
  Support = -> [XY_Plane117]
  sketch-geometry (3):
    g0: LineSegment StartX=0 StartY=0 StartZ=0 EndX=-73.5391 EndY=73.5391 EndZ=0
    g1: Circle CenterX=-73.5391 CenterY=73.5391 CenterZ=0 NormalX=0 NormalY=0 NormalZ=1 AngleXU=0 Radius=2.35
    g2: Circle CenterX=-73.5391 CenterY=73.5391 CenterZ=0 NormalX=0 NormalY=0 NormalZ=1 AngleXU=0 Radius=1.1
  constraints (7):
    c: Coincident(g0,g-1)
    c: Coincident(g1,g0)
    c: Distance(g0) = 104
    c: Diameter(g1) = 4.7
    c: Angle(g0) = 2.35619
    c: Coincident(g2,g1)
    c: Diameter(g2) = 2.2
FEATURE [PartDesign::Pad] Pad079  label="BasePad_Body"
  Direction = (0,0,1)
  Length = 6
  Length2 = 4
  Profile = -> Sketch297
  ReferenceAxis = -> Sketch297 [N_Axis]
  Type = 4
FEATURE [Sketcher::SketchObject] Sketch300  label="BasePad_Hole_Sketch"
  FullyConstrained = true
  MapMode = 5
  Support = -> [XY_Plane117]
  sketch-geometry (2):
    g0: LineSegment StartX=0 StartY=0 StartZ=0 EndX=-73.5391 EndY=73.5391 EndZ=0
    g1: Circle CenterX=-73.5391 CenterY=73.5391 CenterZ=0 NormalX=0 NormalY=0 NormalZ=1 AngleXU=0 Radius=1
  constraints (5):
    c: Coincident(g0,g-1)
    c: Distance(g0) = 104
    c: Angle(g0) = 2.35619
    c: Coincident(g1,g0)
    c: Diameter(g1) = 2
FEATURE [Sketcher::SketchObject] Sketch301  label="BasePad_Cut_Sketch"
  FullyConstrained = true
  MapMode = 5
  Placement = pos=(0,0,0) rot=(1,0,0;1.5708rad)
  Support = -> [XZ_Plane117]
  sketch-geometry (18):
    g0: LineSegment StartX=-96.7 StartY=7 StartZ=0 EndX=-2.84e-14 EndY=7 EndZ=0
    g1: LineSegment StartX=-96.7 StartY=7 StartZ=0 EndX=-96.7 EndY=3 EndZ=0
    g2: LineSegment StartX=-93.7 StartY=3.1e-15 StartZ=0 EndX=-2.84e-14 EndY=3.1e-15 EndZ=0
    g3: LineSegment StartX=-2.84e-14 StartY=3.1e-15 StartZ=0 EndX=-2.84e-14 EndY=7 EndZ=0
    g4: ArcOfCircle CenterX=-93.7 CenterY=3 CenterZ=0 NormalX=0 NormalY=0 NormalZ=1 AngleXU=0 Radius=3 StartAngle=3.14159 EndAngle=4.71239
    g5: LineSegment StartX=-96.7 StartY=3 StartZ=0 EndX=-93.7 EndY=3 EndZ=0
    g6: LineSegment StartX=-93.7 StartY=3 StartZ=0 EndX=-93.7 EndY=3.1e-15 EndZ=0
    g7: LineSegment StartX=-165 StartY=7 StartZ=0 EndX=-98.5 EndY=7 EndZ=0
    g8: LineSegment StartX=-98.5 StartY=7 StartZ=0 EndX=-98.5 EndY=1.8e-15 EndZ=0
    g9: LineSegment StartX=-165 StartY=1.6e-15 StartZ=0 EndX=-165 EndY=7 EndZ=0
    g10: LineSegment StartX=-145.5 StartY=1.6e-15 StartZ=0 EndX=-165 EndY=1.6e-15 EndZ=0
    g11: LineSegment StartX=-98.5 StartY=1.6e-15 StartZ=0 EndX=-110 EndY=1.6e-15 EndZ=0
    g12: LineSegment StartX=-144.1 StartY=-1.4 StartZ=0 EndX=-145.5 EndY=1.6e-15 EndZ=0
    g13: LineSegment StartX=-110 StartY=1.6e-15 StartZ=0 EndX=-111.4 EndY=-1.4 EndZ=0
    g14: LineSegment StartX=-111.4 StartY=-1.4 StartZ=0 EndX=-144.1 EndY=-1.4 EndZ=0
    g15: GeomPoint X=-118.5 Y=1.6e-15 Z=0
    g16: LineSegment StartX=-145.5 StartY=1.6e-15 StartZ=0 EndX=-118.5 EndY=1.6e-15 EndZ=0
    g17: LineSegment StartX=-118.5 StartY=1.6e-15 StartZ=0 EndX=-110 EndY=1.6e-15 EndZ=0
  constraints (49):
    c: Horizontal(g0)
    c: Coincident(g1,g0)
    c: Vertical(g1)
    c: Horizontal(g2)
    c: Coincident(g3,g2)
    c: Coincident(g3,g0)
    c: Vertical(g3)
    c: Coincident(g4,g1)
    c: Coincident(g4,g2)
    c: Coincident(g5,g1)
    c: Coincident(g5,g4)
    c: Coincident(g6,g4)
    c: Coincident(g6,g2)
    c: Coincident(g7,g8)
    c: Coincident(g10,g9)
    c: Coincident(g9,g7)
    c: Horizontal(g7)
    c: Vertical(g8)
    c: Vertical(g9)
    c: Horizontal(g5)
    c: Vertical(g6)
    c: PointOnObject(g7,g0)
    c: DistanceY(g0) = 7
    c: Coincident(g2,g-1)
    c: DistanceY(g6,g6) = 3
    c: PointOnObject(g11,g-1)
    c: DistanceX(g7,g2) = 165
    c: DistanceX(g7,g2) = 98.5
    c: DistanceX(g7,g0) = 1.8
    c: Coincident(g11,g8)
    c: Coincident(g12,g10)
    c: Horizontal(g10)
    c: Coincident(g11,g13)
    c: Horizontal(g11)
    c: Coincident(g14,g12)
    c: Coincident(g13,g14)
    c: Horizontal(g14)
    c: DistanceY(g13,g13) = 1.4
    c: Coincident(g16,g10)
    c: Coincident(g16,g15)
    c: Coincident(g17,g15)
    c: Coincident(g17,g11)
    c: Horizontal(g17)
    c: Horizontal(g16)
    c: DistanceX(g15,g-1) = 118.5
    c: DistanceX(g15,g11) = 8.5
    c: DistanceX(g10,g2) = 145.5
    c: Angle(g14,g12) = 2.35619
    c: Angle(g13,g14) = 2.35619
FEATURE [PartDesign::Groove] Groove008  label="BasePad_Groove"
  Angle = 360
  Axis = (1e-16,1e-16,1)
  Base = (0,0,0)
  BaseFeature = -> Pad079
  Profile = -> Sketch301
  ReferenceAxis = -> Z_Axis117
  Reversed = true
FEATURE [PartDesign::Pad] Pad082  label="BasePad_Pillar"
  BaseFeature = -> Groove008
  Direction = (0,0,1)
  Length = 6
  Length2 = 10
  Profile = -> Sketch298
  ReferenceAxis = -> Sketch298 [N_Axis]
  Type = 0
FEATURE [PartDesign::Chamfer] Chamfer003  label="BasePad_Chamfer"
  Angle = 45
  Base = -> Pad082 [Face2,Edge25,Edge37]
  BaseFeature = -> Pad082
  ChamferType = 0
  FlipDirection = false
  Size = 0.4
  Size2 = 1
  SupportTransform = false
  UseAllEdges = false
FEATURE [PartDesign::Body] Body022063  label="BasePadCorner"
  Group = -> [Sketch297,Sketch298,Pad079,Sketch300,Sketch301,Groove008,Pad082,Chamfer003]
  Origin = -> Origin117
  Placement = pos=(0,0,-153) rot=(0,0,1;0rad)
  Tip = -> Chamfer003
  expr: .Placement.Base.z = <<Common>>#<<Parameters>>.datum_azbase - 10 - 11
COMPONENT P12 — recipe-attached ("SideGuardOut", modeled in this document).
Construction recipe (the document's own serialized feature program — sketch geometry with constraints, then the solid features built on it; lengths are millimeters unless a unit is written):

FEATURE [PartDesign::Plane] DatumPlane051  label="SideGuardOut_DatumPlane_Outer"
  AttachmentOffset = pos=(0,0,11) rot=(0,0,1;0rad)
  Length = 171.251
  MapMode = 5
  Placement = pos=(11,-2.4e-15,2.4e-15) rot=(0.57735,0.57735,0.57735;2.0944rad)
  ResizeMode = 0
  Support = -> [YZ_Plane120]
  Width = 114.566
  expr: .AttachmentOffset.Base.z = <<Common>>#<<Parameters>>.rail_width + 1
FEATURE [PartDesign::ShapeBinder] ShapeBinder014  label="SideGuardOut_ShapeBinder_Rocker"
  Support = -> [Binder]
  TraceSupport = false
FEATURE [PartDesign::Line] DatumLine003  label="SideGuardOut_DatumLine_RockerPivot"
  AttacherType = Attacher::AttachEngineLine
  Length = 20
  MapMode = 19
  Placement = pos=(0,0,215) rot=(0.57735,0.57735,0.57735;2.0944rad)
  ResizeMode = 0
  Support = -> [ShapeBinder014]
FEATURE [Sketcher::SketchObject] Sketch309  label="SideGuardOut_Block_Sketch"
  ExternalGeometry = -> [ShapeBinder014]
  FullyConstrained = true
  MapMode = 5
  Placement = pos=(0,0,0) rot=(0.57735,0.57735,0.57735;2.0944rad)
  Support = -> [YZ_Plane120]
  sketch-geometry (15):
    g0: LineSegment StartX=123 StartY=-10 StartZ=0 EndX=123 EndY=50.2697 EndZ=0
    g1: LineSegment StartX=123 StartY=-10 StartZ=0 EndX=73 EndY=-10 EndZ=0
    g2: LineSegment StartX=73 StartY=-10 StartZ=0 EndX=73 EndY=10 EndZ=0
    g3: ArcOfCircle CenterX=120.5 CenterY=50.2697 CenterZ=0 NormalX=0 NormalY=0 NormalZ=1 AngleXU=0 Radius=2.5 StartAngle=-9e-16 EndAngle=2.17123
    g4: Circle CenterX=113 CenterY=30 CenterZ=0 NormalX=0 NormalY=0 NormalZ=1 AngleXU=0 Radius=2.75
    g5: Circle CenterX=83 CenterY=0 CenterZ=0 NormalX=0 NormalY=0 NormalZ=1 AngleXU=0 Radius=2.75
    g6: Circle CenterX=113 CenterY=0 CenterZ=0 NormalX=0 NormalY=0 NormalZ=1 AngleXU=0 Radius=3.25
    g7: ArcOfCircle CenterX=73 CenterY=40 CenterZ=0 NormalX=0 NormalY=0 NormalZ=1 AngleXU=0 Radius=30 StartAngle=4.71239 EndAngle=6.28313
    g8: ArcOfCircle CenterX=105.5 CenterY=39.9981 CenterZ=0 NormalX=0 NormalY=0 NormalZ=1 AngleXU=0 Radius=2.5 StartAngle=2.17123 EndAngle=3.14153
    g9: LineSegment StartX=0 StartY=215 StartZ=0 EndX=113 EndY=49.9818 EndZ=0
    g10: LineSegment StartX=103 StartY=43.1341 StartZ=0 EndX=123 EndY=56.8295 EndZ=0
    g11: LineSegment StartX=113 StartY=49.9818 StartZ=0 EndX=113.847 EndY=48.7442 EndZ=0
    g12: LineSegment StartX=104.087 StartY=42.0608 StartZ=0 EndX=119.088 EndY=52.3324 EndZ=0
    g13: LineSegment StartX=103 StartY=39.9982 StartZ=0 EndX=103 EndY=43.1341 EndZ=0
    g14: LineSegment StartX=123 StartY=56.8295 StartZ=0 EndX=123 EndY=50.2697 EndZ=0
  constraints (41):
    c: Vertical(g0)
    c: Coincident(g1,g0)
    c: Horizontal(g1)
    c: Coincident(g2,g1)
    c: Vertical(g2)
    c: DistanceY(g0,g-6) = 10
    c: DistanceX(g-6,g0) = 10
    c: Tangent(g0,g3) = -1.5708
    c: Coincident(g4,g-5)
    c: PointOnObject(g5,g-1)
    c: Coincident(g6,g-6)
    c: Diameter(g6) = 6.5
    c: Diameter(g4) = 5.5
    c: Equal(g4,g5)
    c: DistanceX(g5,g6) = 30
    c: DistanceX(g1,g5) = 10
    c: Radius(g3) = 2.5
    c: DistanceY(g2,g2) = 20
    c: Coincident(g7,g2)
    c: Equal(g8,g3)
    c: PointOnObject(g7,g2)
    c: Tangent(g8,g7) = 1.5708
    c: PointOnObject(g9,g-3)
    c: PointOnObject(g9,g-6)
    c: DistanceX(g10,g10) = 20
    c: PointOnObject(g9,g10)
    c: Coincident(g11,g9)
    c: PointOnObject(g11,g12)
    c: Parallel(g11,g9)
    c: Perpendicular(g12,g11)
    c: Tangent(g12,g3) = 1.5708
    c: Tangent(g12,g8) = 1.5708
    c: Distance(g11) = 1.5
    c: Coincident(g9,g-3)
    c: Coincident(g13,g7)
    c: Coincident(g13,g10)
    c: Vertical(g13)
    c: Coincident(g14,g10)
    c: Coincident(g14,g0)
    c: Vertical(g14)
    c: Perpendicular(g9,g10)
FEATURE [Sketcher::SketchObject] Sketch308  label="SideGuardOut_Plate_Sketch"
  ExternalGeometry = -> [ShapeBinder014,Sketch309]
  FullyConstrained = true
  MapMode = 5
  Placement = pos=(11,-2.4e-15,2.4e-15) rot=(0.57735,0.57735,0.57735;2.0944rad)
  Support = -> [DatumPlane051]
  expr: Constraints[3] = <<Common>>#<<Parameters>>.pri_fillet
  sketch-geometry (13):
    g0: LineSegment StartX=123 StartY=-10 StartZ=0 EndX=73 EndY=-10 EndZ=0
    g1: LineSegment StartX=4.77e-14 StartY=215 StartZ=0 EndX=122.939 EndY=57.2468 EndZ=0
    g2: GeomPoint X=118.942 Y=65.7703 Z=0
    g3: Circle CenterX=113 CenterY=3.2e-14 CenterZ=0 NormalX=0 NormalY=0 NormalZ=1 AngleXU=0 Radius=3.25
    g4: ArcOfCircle CenterX=105.5 CenterY=52.9914 CenterZ=0 NormalX=0 NormalY=0 NormalZ=1 AngleXU=0 Radius=2.5 StartAngle=2.14801 EndAngle=3.14159
    g5: ArcOfCircle CenterX=120.5 CenterY=63.8154 CenterZ=0 NormalX=0 NormalY=0 NormalZ=1 AngleXU=0 Radius=2.5 StartAngle=-9e-16 EndAngle=2.24373
    g6: LineSegment StartX=123 StartY=63.8154 StartZ=0 EndX=123 EndY=-10 EndZ=0
    g7: LineSegment StartX=73 StartY=-10 StartZ=0 EndX=73 EndY=10 EndZ=0
    g8: ArcOfCircle CenterX=4.77e-14 CenterY=215 CenterZ=0 NormalX=0 NormalY=0 NormalZ=1 AngleXU=0 Radius=190.831 StartAngle=5.28961 EndAngle=5.38532
    g9: LineSegment StartX=103 StartY=52.9914 StartZ=0 EndX=103 EndY=40 EndZ=0
    g10: ArcOfCircle CenterX=73 CenterY=40 CenterZ=0 NormalX=0 NormalY=0 NormalZ=1 AngleXU=0 Radius=30 StartAngle=4.71239 EndAngle=6.28319
    g11: GeomPoint X=117.303 Y=64.4786 Z=0
    g12: Circle CenterX=113 CenterY=70 CenterZ=0 NormalX=0 NormalY=0 NormalZ=1 AngleXU=0 Radius=6
  constraints (29):
    c: Diameter(g3) = 6.5
    c: Coincident(g7,g0)
    c: Equal(g5,g4)
    c: Radius(g5) = 2.5
    c: Vertical(g6)
    c: Tangent(g5,g6) = 1.5708
    c: Vertical(g7)
    c: Coincident(g6,g0)
    c: Horizontal(g0)
    c: Coincident(g8,g1)
    c: Tangent(g8,g5) = 1.5708
    c: Tangent(g8,g4) = 1.5708
    c: PointOnObject(g1,g-3)
    c: Coincident(g2,g5)
    c: Vertical(g9)
    c: Tangent(g9,g4) = -1.5708
    c: Coincident(g10,g7)
    c: Tangent(g10,g9) = 1.5708
    c: Coincident(g8,g-3)
    c: Coincident(g3,g-4)
    c: Coincident(g-5,g10)
    c: Coincident(g7,g-5)
    c: Coincident(g0,g-6)
    c: PointOnObject(g-4,g1)
    c: PointOnObject(g11,g1)
    c: PointOnObject(g11,g8)
    c: Distance(g11,g-4) = 7
    c: Coincident(g12,g-4)
    c: Diameter(g12) = 12
FEATURE [Sketcher::SketchObject] Sketch310  label="SideGuardOut_SideRail_Sketch"
  ExternalGeometry = -> [ShapeBinder014]
  FullyConstrained = true
  MapMode = 5
  Placement = pos=(0,0,0) rot=(-0.57735,0.57735,0.57735;4.18879rad)
  Support = -> [YZ_Plane120]
  sketch-geometry (22):
    g0: LineSegment StartX=-88 StartY=3 StartZ=0 EndX=-106 EndY=3 EndZ=0
    g1: LineSegment StartX=-106 StartY=3 StartZ=0 EndX=-106 EndY=-3 EndZ=0
    g2: LineSegment StartX=-106 StartY=-3 StartZ=0 EndX=-88 EndY=-3 EndZ=0
    g3: LineSegment StartX=-88 StartY=-3 StartZ=0 EndX=-88 EndY=3 EndZ=0
    g4: LineSegment StartX=-73 StartY=3 StartZ=0 EndX=-78 EndY=3 EndZ=0
    g5: LineSegment StartX=-78 StartY=3 StartZ=0 EndX=-78 EndY=-3 EndZ=0
    g6: LineSegment StartX=-78 StartY=-3 StartZ=0 EndX=-73 EndY=-3 EndZ=0
    g7: LineSegment StartX=-73 StartY=-3 StartZ=0 EndX=-73 EndY=3 EndZ=0
    g8: LineSegment StartX=-88 StartY=0 StartZ=0 EndX=-83 EndY=0 EndZ=0
    g9: LineSegment StartX=-83 StartY=0 StartZ=0 EndX=-78 EndY=0 EndZ=0
    g10: LineSegment StartX=-123 StartY=3 StartZ=0 EndX=-120 EndY=3 EndZ=0
    g11: LineSegment StartX=-120 StartY=3 StartZ=0 EndX=-120 EndY=-3 EndZ=0
    g12: LineSegment StartX=-120 StartY=-3 StartZ=0 EndX=-123 EndY=-3 EndZ=0
    g13: LineSegment StartX=-123 StartY=-3 StartZ=0 EndX=-123 EndY=3 EndZ=0
    g14: LineSegment StartX=-116 StartY=10 StartZ=0 EndX=-110 EndY=10 EndZ=0
    g15: LineSegment StartX=-110 StartY=10 StartZ=0 EndX=-110 EndY=7 EndZ=0
    g16: LineSegment StartX=-110 StartY=7 StartZ=0 EndX=-116 EndY=7 EndZ=0
    g17: LineSegment StartX=-116 StartY=7 StartZ=0 EndX=-116 EndY=10 EndZ=0
    g18: LineSegment StartX=-116 StartY=-7 StartZ=0 EndX=-110 EndY=-7 EndZ=0
    g19: LineSegment StartX=-110 StartY=-7 StartZ=0 EndX=-110 EndY=-10 EndZ=0
    g20: LineSegment StartX=-110 StartY=-10 StartZ=0 EndX=-116 EndY=-10 EndZ=0
    g21: LineSegment StartX=-116 StartY=-10 StartZ=0 EndX=-116 EndY=-7 EndZ=0
  constraints (63):
    c: DistanceX(g-3,g8) = 30
    c: Coincident(g0,g1)
    c: Coincident(g2,g1)
    c: Coincident(g3,g2)
    c: Coincident(g0,g3)
    c: PointOnObject(g8,g3)
    c: Coincident(g8,g9)
    c: Coincident(g5,g6)
    c: Coincident(g6,g7)
    c: Coincident(g4,g7)
    c: Coincident(g4,g5)
    c: Equal(g8,g9)
    c: PointOnObject(g9,g5)
    c: Symmetric(g4,g6,g-1)
    c: DistanceY(g7,g7) = 6
    c: Vertical(g3)
    c: Vertical(g1)
    c: Coincident(g10,g11)
    c: Coincident(g11,g12)
    c: Coincident(g12,g13)
    c: Coincident(g13,g10)
    c: Horizontal(g10)
    c: Horizontal(g12)
    c: Vertical(g11)
    c: Vertical(g13)
    c: Coincident(g14,g15)
    c: Coincident(g15,g16)
    c: Coincident(g16,g17)
    c: Coincident(g17,g14)
    c: Horizontal(g16)
    c: Vertical(g15)
    c: Vertical(g17)
    c: Coincident(g18,g19)
    c: Coincident(g19,g20)
    c: Coincident(g20,g21)
    c: Coincident(g21,g18)
    c: Horizontal(g18)
    c: Horizontal(g20)
    c: Vertical(g19)
    c: Vertical(g21)
    c: Horizontal(g2)
    c: Horizontal(g0)
    c: Horizontal(g8)
    c: Horizontal(g9)
    c: PointOnObject(g9,g-1)
    c: Vertical(g5)
    c: Horizontal(g4)
    c: Horizontal(g6)
    c: Equal(g14,g13)
    c: Equal(g13,g20)
    c: Equal(g20,g3)
    c: Equal(g3,g7)
    c: DistanceX(g8,g4) = 10
    c: Equal(g12,g19)
    c: Equal(g19,g17)
    c: Symmetric(g14,g14,g-4)
    c: Symmetric(g14,g19,g-1)
    c: DistanceY(g20,g14) = 20
    c: PointOnObject(g4,g0)
    c: DistanceX(g10,g-4) = 10
    c: DistanceX(g8,g9) = 10
    c: Symmetric(g0,g10,g-4)
    c: DistanceY(g15,g15) = 3
FEATURE [PartDesign::Pad] Pad084  label="SideGuardOut_Block"
  Direction = (1,-2e-16,3e-16)
  Length = 11
  Length2 = 10
  Placement = pos=(0,0,0) rot=(0.57735,0.57735,0.57735;2.0944rad)
  Profile = -> Sketch309
  ReferenceAxis = -> Sketch309 [N_Axis]
  Type = 0
  expr: Length = <<Common>>#<<Parameters>>.rail_width + 1
FEATURE [PartDesign::Plane] DatumPlane050  label="SideGuardOut_DatumPlane_Channel"
  AttachmentOffset = pos=(0,0,0) rot=(1,0,0;1.5708rad)
  Length = 67.8305
  MapMode = 13
  Placement = pos=(3.66667,114.087,48.9085) rot=(0,0.88459,-0.466369;3.14159rad)
  ResizeMode = 0
  Support = -> [Pad084]
  Width = 176.794
FEATURE [PartDesign::Pad] Pad085  label="SideGuardOut_Plate"
  BaseFeature = -> Pad084
  Direction = (1,-1e-16,1e-16)
  Length = 2
  Length2 = 10
  Placement = pos=(0,0,0) rot=(0.57735,0.57735,0.57735;2.0944rad)
  Profile = -> Sketch308
  ReferenceAxis = -> Sketch308 [N_Axis]
  Type = 0
  expr: Length = Common#<<Parameters>>.rocker_plate
FEATURE [PartDesign::Pad] Pad086  label="SideGuardOut_SideRail"
  BaseFeature = -> Pad085
  Direction = (-1,2e-16,-3e-16)
  Length = 3
  Length2 = 10
  Placement = pos=(0,0,0) rot=(0.57735,0.57735,0.57735;2.0944rad)
  Profile = -> Sketch310
  ReferenceAxis = -> Sketch310 [N_Axis]
  Type = 0
FEATURE [Sketcher::SketchObject] Sketch314  label="SideGuardOut_SideBolt_Sketch"
  AttachmentOffset = pos=(0,0,2) rot=(0,0,1;0rad)
  ExternalGeometry = -> [ShapeBinder014]
  FullyConstrained = true
  MapMode = 5
  Placement = pos=(13,-2.7e-15,2.7e-15) rot=(0.57735,0.57735,0.57735;2.0944rad)
  Support = -> [DatumPlane051]
  expr: .AttachmentOffset.Base.z = <<Common>>#<<Parameters>>.rocker_plate
  sketch-geometry (2):
    g0: Circle CenterX=83 CenterY=0 CenterZ=0 NormalX=0 NormalY=0 NormalZ=1 AngleXU=0 Radius=2.75
    g1: Circle CenterX=113 CenterY=0 CenterZ=0 NormalX=0 NormalY=0 NormalZ=1 AngleXU=0 Radius=3.25
  constraints (5):
    c: PointOnObject(g0,g-1)
    c: Diameter(g0) = 5.5
    c: Coincident(g1,g-3)
    c: Diameter(g1) = 6.5
    c: DistanceX(g0,g1) = 30
FEATURE [Sketcher::SketchObject] Sketch315  label="SideGuardOut_CounterBoreSide_Sketch"
  AttachmentOffset = pos=(0,0,2) rot=(0,0,1;0rad)
  ExternalGeometry = -> [Sketch314]
  FullyConstrained = true
  MapMode = 5
  Placement = pos=(13,-2.7e-15,2.7e-15) rot=(0.57735,0.57735,0.57735;2.0944rad)
  Support = -> [DatumPlane051]
  expr: .AttachmentOffset.Base.z = <<Common>>#<<Parameters>>.rocker_plate
  sketch-geometry (1):
    g0: Circle CenterX=83 CenterY=-9.3e-15 CenterZ=0 NormalX=0 NormalY=0 NormalZ=1 AngleXU=0 Radius=5
  constraints (2):
    c: Diameter(g0) = 10
    c: Coincident(g0,g-3)
FEATURE [Sketcher::SketchObject] Sketch316  label="SideGuardOut_CBSSupport_Sketch"
  AttachmentOffset = pos=(0,0,-7) rot=(0,0,1;0rad)
  ExternalGeometry = -> [Sketch314,Sketch315]
  FullyConstrained = true
  MapMode = 5
  Placement = pos=(4,-1.7e-15,1.7e-15) rot=(0.57735,0.57735,0.57735;2.0944rad)
  Support = -> [DatumPlane051]
  expr: .AttachmentOffset.Base.z = -(<<Common>>#<<Parameters>>.rail_width + 1 - 4)
  sketch-geometry (12):
    g0: LineSegment StartX=78.8242 StartY=2.75 StartZ=0 EndX=87.1758 EndY=2.75 EndZ=0
    g1: LineSegment StartX=87.4695 StartY=2.24137 StartZ=0 EndX=83.2937 EndY=-4.99137 EndZ=0
    g2: LineSegment StartX=82.7063 StartY=-4.99137 StartZ=0 EndX=78.5305 EndY=2.24137 EndZ=0
    g3: ArcOfCircle CenterX=83 CenterY=-9.2e-15 CenterZ=0 NormalX=0 NormalY=0 NormalZ=1 AngleXU=0 Radius=5 StartAngle=2.55923 EndAngle=2.67676
    g4: ArcOfCircle CenterX=83 CenterY=-9.2e-15 CenterZ=0 NormalX=0 NormalY=0 NormalZ=1 AngleXU=0 Radius=5 StartAngle=0.464833 EndAngle=0.582364
    g5: ArcOfCircle CenterX=83 CenterY=-9.2e-15 CenterZ=0 NormalX=0 NormalY=0 NormalZ=1 AngleXU=0 Radius=5 StartAngle=4.65362 EndAngle=4.77115
    g6: LineSegment StartX=83 StartY=-9.2e-15 StartZ=0 EndX=83 EndY=2.75 EndZ=0
    g7: LineSegment StartX=83 StartY=-9.2e-15 StartZ=0 EndX=85.3816 EndY=-1.375 EndZ=0
    g8: LineSegment StartX=83 StartY=-9.2e-15 StartZ=0 EndX=80.6184 EndY=-1.375 EndZ=0
    g9: LineSegment StartX=85.3816 StartY=-1.375 StartZ=0 EndX=80.6184 EndY=-1.375 EndZ=0
    g10: LineSegment StartX=80.6184 StartY=-1.375 StartZ=0 EndX=83 EndY=2.75 EndZ=0
    g11: LineSegment StartX=83 StartY=2.75 StartZ=0 EndX=85.3816 EndY=-1.375 EndZ=0
  constraints (33):
    c: Horizontal(g0)
    c: Coincident(g3,g2)
    c: Coincident(g3,g0)
    c: Coincident(g4,g3)
    c: Coincident(g4,g0)
    c: Coincident(g4,g1)
    c: Coincident(g5,g3)
    c: Coincident(g5,g1)
    c: Coincident(g5,g2)
    c: Coincident(g6,g3)
    c: PointOnObject(g6,g0)
    c: Vertical(g6)
    c: Coincident(g7,g3)
    c: Coincident(g8,g3)
    c: PointOnObject(g8,g2)
    c: Coincident(g9,g7)
    c: Coincident(g9,g8)
    c: Coincident(g10,g8)
    c: Coincident(g10,g6)
    c: Coincident(g11,g6)
    c: Coincident(g11,g7)
    c: Horizontal(g9)
    c: Equal(g11,g9)
    c: Perpendicular(g2,g8)
    c: Perpendicular(g1,g7)
    c: Equal(g10,g11)
    c: PointOnObject(g7,g1)
    c: PointOnObject(g0,g-4)
    c: PointOnObject(g2,g-4)
    c: PointOnObject(g0,g-4)
    c: PointOnObject(g6,g-3)
    c: PointOnObject(g7,g-3)
    c: Coincident(g3,g-4)
FEATURE [Sketcher::SketchObject] Sketch317  label="SideGuardOut_Channel_Sketch"
  ExternalGeometry = -> [Pad084]
  FullyConstrained = true
  MapMode = 5
  Placement = pos=(3.66667,114.087,48.9085) rot=(0,0.88459,-0.466369;3.14159rad)
  Support = -> [DatumPlane050]
  sketch-geometry (6):
    g0: LineSegment StartX=-4.63333 StartY=6.6 StartZ=0 EndX=0.966667 EndY=6.6 EndZ=0
    g1: LineSegment StartX=0.966667 StartY=6.6 StartZ=0 EndX=0.966667 EndY=5 EndZ=0
    g2: LineSegment StartX=0.966667 StartY=5 StartZ=0 EndX=-4.63333 EndY=5 EndZ=0
    g3: LineSegment StartX=-4.63333 StartY=5 StartZ=0 EndX=-4.63333 EndY=6.6 EndZ=0
    g4: LineSegment StartX=-4.63333 StartY=5 StartZ=0 EndX=-7.33333 EndY=5 EndZ=0
    g5: LineSegment StartX=0.966667 StartY=5 StartZ=0 EndX=3.66667 EndY=5 EndZ=0
  constraints (18):
    c: Coincident(g0,g1)
    c: Coincident(g1,g2)
    c: Coincident(g2,g3)
    c: Coincident(g3,g0)
    c: Horizontal(g0)
    c: Horizontal(g2)
    c: Vertical(g1)
    c: Vertical(g3)
    c: Coincident(g4,g2)
    c: Horizontal(g4)
    c: Coincident(g5,g1)
    c: Horizontal(g5)
    c: Equal(g4,g5)
    c: DistanceX(g2,g2) = 5.6
    c: DistanceY(g1,g1) = 1.6
    c: DistanceY(g-1,g1) = 5
    c: PointOnObject(g4,g-3)
    c: PointOnObject(g5,g-4)
FEATURE [Sketcher::SketchObject] Sketch318  label="SideGuardOut_UpperCatch_Sketch"
  ExternalGeometry = -> [ShapeBinder014]
  FullyConstrained = true
  MapMode = 5
  Placement = pos=(0,0,0) rot=(0.57735,0.57735,0.57735;2.0944rad)
  Support = -> [YZ_Plane120]
  sketch-geometry (4):
    g0: LineSegment StartX=105 StartY=30 StartZ=0 EndX=121 EndY=30 EndZ=0
    g1: LineSegment StartX=121 StartY=30 StartZ=0 EndX=121 EndY=26 EndZ=0
    g2: LineSegment StartX=121 StartY=26 StartZ=0 EndX=105 EndY=26 EndZ=0
    g3: LineSegment StartX=105 StartY=26 StartZ=0 EndX=105 EndY=30 EndZ=0
  constraints (11):
    c: Coincident(g0,g1)
    c: Coincident(g1,g2)
    c: Coincident(g2,g3)
    c: Coincident(g3,g0)
    c: Horizontal(g2)
    c: Vertical(g1)
    c: Vertical(g3)
    c: Symmetric(g0,g0,g-4)
    c: DistanceY(g1,g1) = 4
    c: DistanceX(g2,g2) = 16
    c: PointOnObject(g-3,g0)
FEATURE [PartDesign::Pad] Pad087  label="SideGuardOut_Catch"
  BaseFeature = -> Pad086
  Direction = (1,-2e-16,3e-16)
  Length = 3
  Length2 = 10
  Placement = pos=(0,0,0) rot=(0.57735,0.57735,0.57735;2.0944rad)
  Profile = -> Sketch318
  ReferenceAxis = -> Sketch318 [N_Axis]
  Reversed = true
  Type = 0
FEATURE [Sketcher::SketchObject] Sketch321  label="SideGuardOut_CornerBolt_Sketch"
  AttachmentOffset = pos=(0,0,2) rot=(0,0,1;0rad)
  ExternalGeometry = -> [ShapeBinder014]
  FullyConstrained = true
  MapMode = 5
  Placement = pos=(13,-2.7e-15,2.7e-15) rot=(0.57735,0.57735,0.57735;2.0944rad)
  Support = -> [DatumPlane051]
  expr: .AttachmentOffset.Base.z = <<Common>>#<<Parameters>>.rocker_plate
  sketch-geometry (1):
    g0: Circle CenterX=113 CenterY=0 CenterZ=0 NormalX=0 NormalY=0 NormalZ=1 AngleXU=0 Radius=3.25
  constraints (2):
    c: Coincident(g0,g-3)
    c: Diameter(g0) = 6.5
FEATURE [Sketcher::SketchObject] Sketch319  label="SideGuardOut_CounterBoreCorner_Sketch"
  AttachmentOffset = pos=(0,0,2) rot=(0,0,1;0rad)
  ExternalGeometry = -> [Sketch321]
  FullyConstrained = true
  MapMode = 5
  Placement = pos=(13,-2.7e-15,2.7e-15) rot=(0.57735,0.57735,0.57735;2.0944rad)
  Support = -> [DatumPlane051]
  expr: .AttachmentOffset.Base.z = <<Common>>#<<Parameters>>.rocker_plate
  sketch-geometry (1):
    g0: Circle CenterX=113 CenterY=-1.25e-14 CenterZ=0 NormalX=0 NormalY=0 NormalZ=1 AngleXU=0 Radius=6
  constraints (2):
    c: Diameter(g0) = 12
    c: Coincident(g0,g-3)
FEATURE [Sketcher::SketchObject] Sketch320  label="SideGuardOut_CBCSupport_Sketch"
  AttachmentOffset = pos=(0,0,-3) rot=(0,0,1;0rad)
  ExternalGeometry = -> [Sketch321,Sketch319]
  FullyConstrained = true
  MapMode = 5
  Placement = pos=(8,-2.1e-15,2.1e-15) rot=(0.57735,0.57735,0.57735;2.0944rad)
  Support = -> [DatumPlane051]
  expr: .AttachmentOffset.Base.z = <<Common>>#<<Parameters>>.rocker_plate - 5
  sketch-geometry (12):
    g0: LineSegment StartX=107.956 StartY=3.25 StartZ=0 EndX=118.044 EndY=3.25 EndZ=0
    g1: LineSegment StartX=118.336 StartY=2.74285 StartZ=0 EndX=113.293 EndY=-5.99285 EndZ=0
    g2: LineSegment StartX=112.707 StartY=-5.99285 StartZ=0 EndX=107.664 EndY=2.74285 EndZ=0
    g3: ArcOfCircle CenterX=113 CenterY=-2.51e-14 CenterZ=0 NormalX=0 NormalY=0 NormalZ=1 AngleXU=0 Radius=6 StartAngle=2.56917 EndAngle=2.66681
    g4: ArcOfCircle CenterX=113 CenterY=-2.51e-14 CenterZ=0 NormalX=0 NormalY=0 NormalZ=1 AngleXU=0 Radius=6 StartAngle=0.474779 EndAngle=0.572419
    g5: ArcOfCircle CenterX=113 CenterY=-2.51e-14 CenterZ=0 NormalX=0 NormalY=0 NormalZ=1 AngleXU=0 Radius=6 StartAngle=4.66357 EndAngle=4.76121
    g6: LineSegment StartX=113 StartY=-2.51e-14 StartZ=0 EndX=113 EndY=3.25 EndZ=0
    g7: LineSegment StartX=113 StartY=-2.51e-14 StartZ=0 EndX=110.185 EndY=-1.625 EndZ=0
    g8: LineSegment StartX=113 StartY=-2.51e-14 StartZ=0 EndX=115.815 EndY=-1.625 EndZ=0
    g9: LineSegment StartX=115.815 StartY=-1.625 StartZ=0 EndX=110.185 EndY=-1.625 EndZ=0
    g10: LineSegment StartX=110.185 StartY=-1.625 StartZ=0 EndX=113 EndY=3.25 EndZ=0
    g11: LineSegment StartX=113 StartY=3.25 StartZ=0 EndX=115.815 EndY=-1.625 EndZ=0
  constraints (33):
    c: Horizontal(g0)
    c: Coincident(g3,g2)
    c: Coincident(g3,g0)
    c: Coincident(g4,g3)
    c: Coincident(g4,g0)
    c: Coincident(g4,g1)
    c: Coincident(g5,g3)
    c: Coincident(g5,g1)
    c: Coincident(g5,g2)
    c: Coincident(g6,g3)
    c: PointOnObject(g6,g0)
    c: Vertical(g6)
    c: Coincident(g7,g3)
    c: PointOnObject(g7,g2)
    c: Coincident(g8,g3)
    c: PointOnObject(g8,g1)
    c: Coincident(g9,g8)
    c: Coincident(g9,g7)
    c: Perpendicular(g2,g7)
    c: Perpendicular(g1,g8)
    c: Coincident(g10,g7)
    c: Coincident(g10,g6)
    c: Coincident(g11,g6)
    c: Coincident(g11,g8)
    c: Equal(g10,g11)
    c: Equal(g11,g9)
    c: Horizontal(g9)
    c: PointOnObject(g0,g-4)
    c: PointOnObject(g2,g-4)
    c: PointOnObject(g1,g-4)
    c: Coincident(g3,g-4)
    c: PointOnObject(g8,g-3)
    c: PointOnObject(g6,g-3)
FEATURE [PartDesign::Pocket] Pocket  label="SideGuardOut_CornerBolt"
  BaseFeature = -> Pad087
  Direction = (-1,1e-16,-1e-16)
  Length = 5
  Length2 = 5
  Midplane = true
  Placement = pos=(0,0,0) rot=(0.57735,0.57735,0.57735;2.0944rad)
  Profile = -> Sketch321
  ReferenceAxis = -> Sketch321 [N_Axis]
  Type = 1
FEATURE [PartDesign::Pocket] Pocket181  label="SideGuardOut_CounterBoreCorner"
  BaseFeature = -> Pocket
  Direction = (-1,1e-16,-1e-16)
  Length = 5
  Length2 = 5
  Placement = pos=(0,0,0) rot=(0.57735,0.57735,0.57735;2.0944rad)
  Profile = -> Sketch319
  ReferenceAxis = -> Sketch319 [N_Axis]
  Type = 0
FEATURE [PartDesign::Pocket] Pocket182  label="SudeGuardOut_SideBolt"
  BaseFeature = -> Pocket181
  Direction = (-1,1e-16,-1e-16)
  Length = 5
  Length2 = 5
  Midplane = true
  Placement = pos=(0,0,0) rot=(0.57735,0.57735,0.57735;2.0944rad)
  Profile = -> Sketch314
  ReferenceAxis = -> Sketch314 [N_Axis]
  Type = 1
FEATURE [PartDesign::Pocket] Pocket183  label="SideGuardOut_CountreBoreSide"
  BaseFeature = -> Pocket182
  Direction = (-1,1e-16,-1e-16)
  Length = 9
  Length2 = 5
  Placement = pos=(0,0,0) rot=(0.57735,0.57735,0.57735;2.0944rad)
  Profile = -> Sketch315
  ReferenceAxis = -> Sketch315 [N_Axis]
  Type = 0
  expr: Length = <<Common>>#<<Parameters>>.rail_width + 1 + <<Common>>#<<Parameters>>.rocker_plate - 4
FEATURE [PartDesign::Pocket] Pocket184  label="SideGuardOut_Channel"
  BaseFeature = -> Pocket183
  Direction = (0,0.825091,0.565)
  Length = 5
  Length2 = 5
  Midplane = true
  Placement = pos=(0,0,0) rot=(0.57735,0.57735,0.57735;2.0944rad)
  Profile = -> Sketch317
  ReferenceAxis = -> Sketch317 [N_Axis]
  Type = 1
FEATURE [PartDesign::Fillet] Fillet012  label="SideGuardOut_Fillet"
  Base = -> Pocket184 [Edge1,Edge46,Edge68,Edge11,Edge135,Edge62]
  BaseFeature = -> Pocket184
  Placement = pos=(0,0,0) rot=(0.57735,0.57735,0.57735;2.0944rad)
  Radius = 1
  SupportTransform = false
  UseAllEdges = false
FEATURE [PartDesign::Chamfer] Chamfer  label="SideGuardOut_Chamfer"
  Angle = 45
  Base = -> Fillet012 [Face44]
  BaseFeature = -> Fillet012
  ChamferType = 0
  FlipDirection = false
  Placement = pos=(0,0,0) rot=(0.57735,0.57735,0.57735;2.0944rad)
  Size = 0.45
  Size2 = 1
  SupportTransform = false
  UseAllEdges = false
FEATURE [PartDesign::Pocket] Pocket185  label="SideGuardOut_CBCSupport"
  BaseFeature = -> Chamfer
  Direction = (-1,1e-16,-1e-16)
  Length = 0.2
  Length2 = 5
  Placement = pos=(0,0,0) rot=(0.57735,0.57735,0.57735;2.0944rad)
  Profile = -> Sketch320
  ReferenceAxis = -> Sketch320 [N_Axis]
  Type = 0
FEATURE [PartDesign::Pocket] Pocket186  label="SideGuardOut_CBSSupport"
  BaseFeature = -> Pocket185
  Direction = (-1,1e-16,-1e-16)
  Length = 0.2
  Length2 = 5
  Placement = pos=(0,0,0) rot=(0.57735,0.57735,0.57735;2.0944rad)
  Profile = -> Sketch316
  ReferenceAxis = -> Sketch316 [N_Axis]
  Type = 0
FEATURE [PartDesign::Body] Body022065  label="SideGuardOut"
  Group = -> [ShapeBinder014,Sketch309,Sketch310,Sketch308,DatumLine003,DatumPlane050,Pad084,Pad085,Pad086,Sketch314,Sketch315,Sketch316,DatumPlane051,Sketch317,Sketch318,Sketch319,Sketch320,Pad087,Sketch321,Pocket,Pocket181,Pocket182,Pocket183,Pocket184,Fillet012,Chamfer,Pocket185,Pocket186]
  Origin = -> Origin119
  Placement = pos=(123,0,-132) rot=(0,0,1;0rad)
  Tip = -> Pocket186
  expr: .Placement.Base.x = <<Common>>#<<Parameters>>.boxsize_x / 2
  expr: .Placement.Base.z = <<Common>>#<<Parameters>>.datum_azbase
